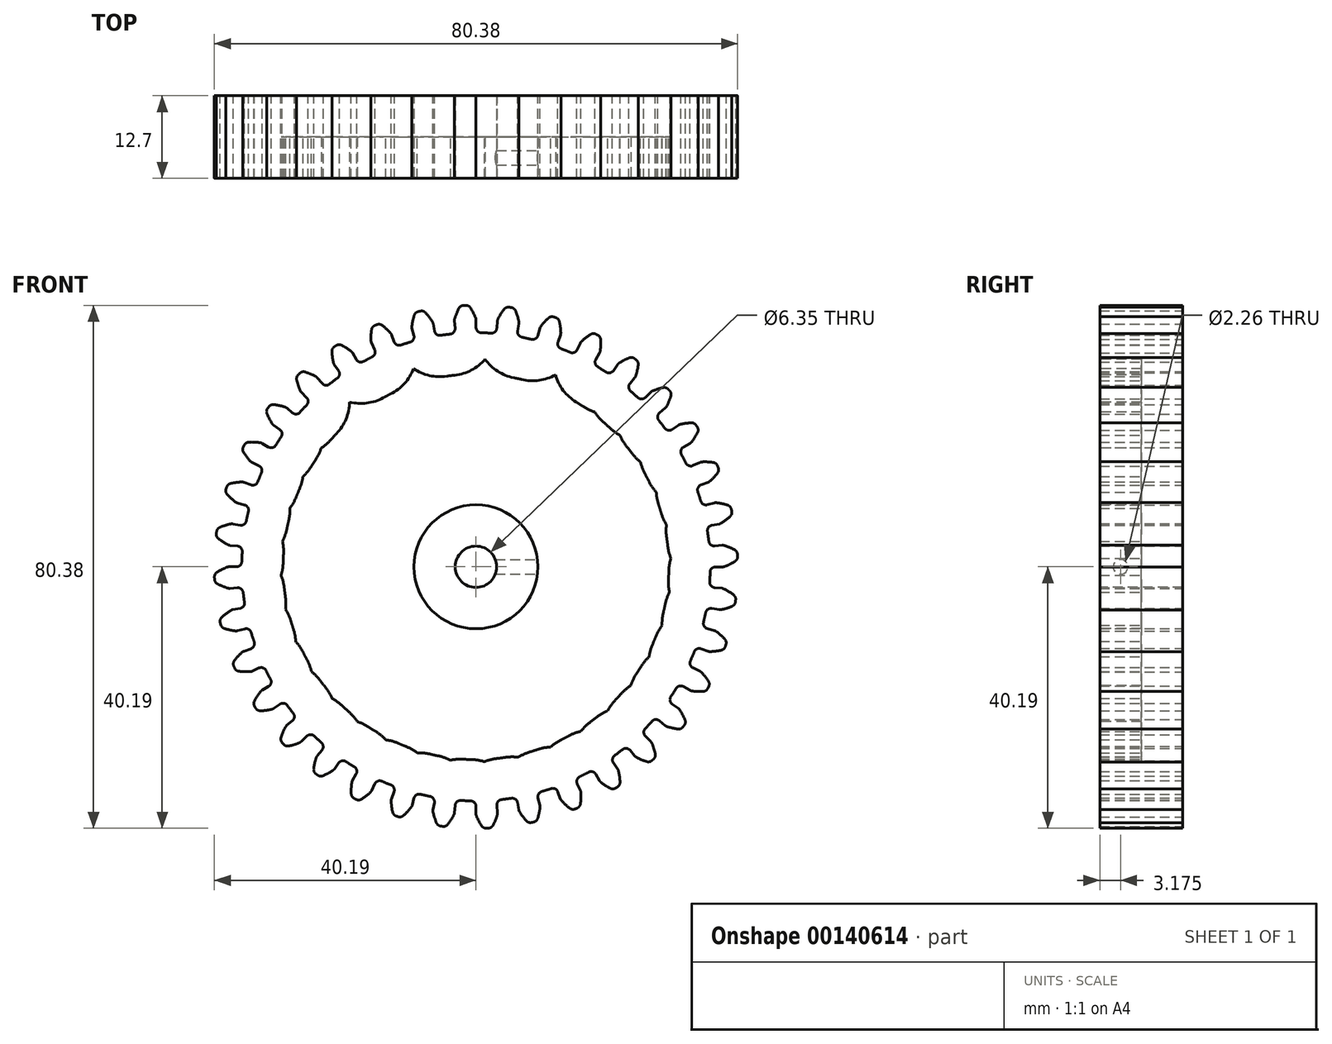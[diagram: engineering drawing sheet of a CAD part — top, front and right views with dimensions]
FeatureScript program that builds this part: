
annotation { "Feature Type Name" : "Feature", "Feature Type Description" : "" }
export const myFeature = defineFeature(function(context is Context, id is Id, definition is map)
    precondition{}
    {
        {
            var Q0;
            Q0=qCreatedBy(makeId("Front.planeOp"),FACE);
            var sketch = newSketch(context, id + "F0", { "sketchPlane" : qUnion([Q0])});
            skArc(sketch, "E0", {"start": v(-3.95, 35.77) * mm, "mid": v(-4.7, 35.68) * mm, "end": v(-5.45, 35.57) * mm});
            skArc(sketch, "E1", {"start": v(-0.05, 38.25) * mm, "mid": v(-0.42, 39.05) * mm, "end": v(-0.85, 39.8) * mm});
            skArc(sketch, "E2.trimOffspring", {"start": v(-1.58, 40.19) * mm, "mid": v(-1.67, 40.18) * mm, "end": v(-1.75, 40.18) * mm});
            skLineSegment(sketch, "E3", {"start": v(0, 37.94) * mm, "end": v(0, 36.8) * mm});
            skArc(sketch, "E4.MirrorCS", {"start": v(-1.93, 40.17) * mm, "mid": v(-1.84, 40.17) * mm, "end": v(-1.75, 40.18) * mm});
            skArc(sketch, "E5.MirrorCS", {"start": v(-3.28, 38.11) * mm, "mid": v(-2.99, 38.93) * mm, "end": v(-2.62, 39.73) * mm});
            skLineSegment(sketch, "E6.MirrorCS", {"start": v(-3.31, 37.8) * mm, "end": v(-3.21, 36.66) * mm});
            skPoint(sketch, "E7.visualSharp", {"position": v(-3.33, 37.95) * mm});
            skArc(sketch, "E7.filletArc", {"start": v(-3.28, 38.11) * mm, "mid": v(-3.31, 37.96) * mm, "end": v(-3.31, 37.8) * mm});
            skPoint(sketch, "E8.visualSharp", {"position": v(0, 38.1) * mm});
            skArc(sketch, "E8.filletArc", {"start": v(0, 37.94) * mm, "mid": v(0, 38.1) * mm, "end": v(-0.05, 38.25) * mm});
            skPoint(sketch, "E9.visualSharp", {"position": v(-2.39, 40.15) * mm});
            skArc(sketch, "E9.filletArc", {"start": v(-1.93, 40.17) * mm, "mid": v(-2.33, 40.04) * mm, "end": v(-2.62, 39.73) * mm});
            skPoint(sketch, "E10.visualSharp", {"position": v(-1.12, 40.2) * mm});
            skArc(sketch, "E10.filletArc", {"start": v(-0.85, 39.8) * mm, "mid": v(-1.17, 40.1) * mm, "end": v(-1.58, 40.19) * mm});
            skPoint(sketch, "E11.visualSharp", {"position": v(-3.14, 35.85) * mm});
            skArc(sketch, "E11.filletArc", {"start": v(-3.95, 35.77) * mm, "mid": v(-3.4, 36.06) * mm, "end": v(-3.21, 36.66) * mm});
            skPoint(sketch, "E12.visualSharp", {"position": v(0, 35.98) * mm});
            skArc(sketch, "E12.filletArc", {"start": v(0, 36.8) * mm, "mid": v(0.24, 36.22) * mm, "end": v(0.81, 35.97) * mm});
            skArc(sketch, "E13.1.0", {"start": v(-10.1, 34.54) * mm, "mid": v(-9.6, 34.93) * mm, "end": v(-9.53, 35.54) * mm});
            skLineSegment(sketch, "E13.1.1", {"start": v(-9.83, 36.65) * mm, "end": v(-9.53, 35.54) * mm});
            skArc(sketch, "E13.1.2", {"start": v(-9.85, 36.96) * mm, "mid": v(-9.85, 36.8) * mm, "end": v(-9.83, 36.65) * mm});
            skArc(sketch, "E13.1.3", {"start": v(-9.85, 36.96) * mm, "mid": v(-9.7, 37.82) * mm, "end": v(-9.48, 38.67) * mm});
            skArc(sketch, "E13.1.4", {"start": v(-8.87, 39.23) * mm, "mid": v(-9.25, 39.03) * mm, "end": v(-9.48, 38.67) * mm});
            skArc(sketch, "E13.1.5", {"start": v(-8.87, 39.23) * mm, "mid": v(-8.79, 39.24) * mm, "end": v(-8.7, 39.26) * mm});
            skArc(sketch, "E13.1.6", {"start": v(-8.54, 39.3) * mm, "mid": v(-8.62, 39.28) * mm, "end": v(-8.7, 39.26) * mm});
            skArc(sketch, "E13.1.7", {"start": v(-7.75, 39.05) * mm, "mid": v(-8.11, 39.28) * mm, "end": v(-8.54, 39.3) * mm});
            skArc(sketch, "E13.1.8", {"start": v(-6.7, 37.66) * mm, "mid": v(-7.2, 38.38) * mm, "end": v(-7.75, 39.05) * mm});
            skArc(sketch, "E13.1.9", {"start": v(-6.58, 37.37) * mm, "mid": v(-6.62, 37.52) * mm, "end": v(-6.7, 37.66) * mm});
            skLineSegment(sketch, "E13.1.10", {"start": v(-6.58, 37.37) * mm, "end": v(-6.38, 36.24) * mm});
            skArc(sketch, "E13.1.11", {"start": v(-6.38, 36.24) * mm, "mid": v(-6.05, 35.71) * mm, "end": v(-5.45, 35.57) * mm});
            skArc(sketch, "E13.2.0", {"start": v(-15.94, 32.26) * mm, "mid": v(-15.53, 32.73) * mm, "end": v(-15.56, 33.35) * mm});
            skLineSegment(sketch, "E13.2.1", {"start": v(-16.04, 34.39) * mm, "end": v(-15.56, 33.35) * mm});
            skArc(sketch, "E13.2.2", {"start": v(-16.12, 34.7) * mm, "mid": v(-16.1, 34.53) * mm, "end": v(-16.04, 34.39) * mm});
            skArc(sketch, "E13.2.3", {"start": v(-16.12, 34.7) * mm, "mid": v(-16.12, 35.56) * mm, "end": v(-16.05, 36.44) * mm});
            skArc(sketch, "E13.2.4", {"start": v(-15.55, 37.09) * mm, "mid": v(-15.89, 36.83) * mm, "end": v(-16.05, 36.44) * mm});
            skArc(sketch, "E13.2.5", {"start": v(-15.55, 37.09) * mm, "mid": v(-15.47, 37.12) * mm, "end": v(-15.4, 37.16) * mm});
            skArc(sketch, "E13.2.6", {"start": v(-15.23, 37.22) * mm, "mid": v(-15.31, 37.19) * mm, "end": v(-15.4, 37.16) * mm});
            skArc(sketch, "E13.2.7", {"start": v(-14.42, 37.11) * mm, "mid": v(-14.8, 37.28) * mm, "end": v(-15.23, 37.22) * mm});
            skArc(sketch, "E13.2.8", {"start": v(-13.13, 35.93) * mm, "mid": v(-13.75, 36.55) * mm, "end": v(-14.42, 37.11) * mm});
            skArc(sketch, "E13.2.9", {"start": v(-12.97, 35.66) * mm, "mid": v(-13.04, 35.8) * mm, "end": v(-13.13, 35.93) * mm});
            skLineSegment(sketch, "E13.2.10", {"start": v(-12.97, 35.66) * mm, "end": v(-12.58, 34.58) * mm});
            skArc(sketch, "E13.2.11", {"start": v(-12.58, 34.58) * mm, "mid": v(-12.16, 34.12) * mm, "end": v(-11.54, 34.08) * mm});
            skArc(sketch, "E13.3.0", {"start": v(-21.3, 29) * mm, "mid": v(-20.97, 29.53) * mm, "end": v(-21.11, 30.14) * mm});
            skLineSegment(sketch, "E13.3.1", {"start": v(-21.77, 31.08) * mm, "end": v(-21.11, 30.14) * mm});
            skArc(sketch, "E13.3.2", {"start": v(-21.9, 31.37) * mm, "mid": v(-21.85, 31.21) * mm, "end": v(-21.77, 31.08) * mm});
            skArc(sketch, "E13.3.3", {"start": v(-21.9, 31.37) * mm, "mid": v(-22.05, 32.22) * mm, "end": v(-22.13, 33.1) * mm});
            skArc(sketch, "E13.3.4", {"start": v(-21.75, 33.83) * mm, "mid": v(-22.04, 33.51) * mm, "end": v(-22.13, 33.1) * mm});
            skArc(sketch, "E13.3.5", {"start": v(-21.75, 33.83) * mm, "mid": v(-21.68, 33.87) * mm, "end": v(-21.6, 33.92) * mm});
            skArc(sketch, "E13.3.6", {"start": v(-21.46, 34.01) * mm, "mid": v(-21.54, 33.96) * mm, "end": v(-21.6, 33.92) * mm});
            skArc(sketch, "E13.3.7", {"start": v(-20.64, 34.05) * mm, "mid": v(-21.06, 34.14) * mm, "end": v(-21.46, 34.01) * mm});
            skArc(sketch, "E13.3.8", {"start": v(-19.17, 33.1) * mm, "mid": v(-19.88, 33.6) * mm, "end": v(-20.64, 34.05) * mm});
            skArc(sketch, "E13.3.9", {"start": v(-18.97, 32.86) * mm, "mid": v(-19.06, 33) * mm, "end": v(-19.17, 33.1) * mm});
            skLineSegment(sketch, "E13.3.10", {"start": v(-18.97, 32.86) * mm, "end": v(-18.4, 31.87) * mm});
            skArc(sketch, "E13.3.11", {"start": v(-18.4, 31.87) * mm, "mid": v(-17.9, 31.5) * mm, "end": v(-17.28, 31.56) * mm});
            skArc(sketch, "E13.4.0", {"start": v(-26.01, 24.86) * mm, "mid": v(-25.78, 25.44) * mm, "end": v(-26.03, 26.02) * mm});
            skLineSegment(sketch, "E13.4.1", {"start": v(-26.84, 26.82) * mm, "end": v(-26.03, 26.02) * mm});
            skArc(sketch, "E13.4.2", {"start": v(-27.01, 27.09) * mm, "mid": v(-26.94, 26.95) * mm, "end": v(-26.84, 26.82) * mm});
            skArc(sketch, "E13.4.3", {"start": v(-27.01, 27.09) * mm, "mid": v(-27.32, 27.9) * mm, "end": v(-27.54, 28.75) * mm});
            skArc(sketch, "E13.4.4", {"start": v(-27.3, 29.53) * mm, "mid": v(-27.52, 29.17) * mm, "end": v(-27.54, 28.75) * mm});
            skArc(sketch, "E13.4.5", {"start": v(-27.3, 29.53) * mm, "mid": v(-27.23, 29.6) * mm, "end": v(-27.17, 29.65) * mm});
            skArc(sketch, "E13.4.6", {"start": v(-27.04, 29.77) * mm, "mid": v(-27.1, 29.7) * mm, "end": v(-27.17, 29.65) * mm});
            skArc(sketch, "E13.4.7", {"start": v(-26.24, 29.94) * mm, "mid": v(-26.66, 29.96) * mm, "end": v(-27.04, 29.77) * mm});
            skArc(sketch, "E13.4.8", {"start": v(-24.63, 29.27) * mm, "mid": v(-25.42, 29.64) * mm, "end": v(-26.24, 29.94) * mm});
            skArc(sketch, "E13.4.9", {"start": v(-24.38, 29.07) * mm, "mid": v(-24.5, 29.18) * mm, "end": v(-24.63, 29.27) * mm});
            skLineSegment(sketch, "E13.4.10", {"start": v(-24.38, 29.07) * mm, "end": v(-23.65, 28.2) * mm});
            skArc(sketch, "E13.4.11", {"start": v(-23.65, 28.2) * mm, "mid": v(-23.1, 27.9) * mm, "end": v(-22.5, 28.08) * mm});
            skArc(sketch, "E13.5.0", {"start": v(-29.94, 19.97) * mm, "mid": v(-29.81, 20.58) * mm, "end": v(-30.15, 21.1) * mm});
            skLineSegment(sketch, "E13.5.1", {"start": v(-31.09, 21.76) * mm, "end": v(-30.15, 21.1) * mm});
            skArc(sketch, "E13.5.2", {"start": v(-31.3, 21.98) * mm, "mid": v(-31.2, 21.86) * mm, "end": v(-31.09, 21.76) * mm});
            skArc(sketch, "E13.5.3", {"start": v(-31.3, 21.98) * mm, "mid": v(-31.75, 22.74) * mm, "end": v(-32.12, 23.53) * mm});
            skArc(sketch, "E13.5.4", {"start": v(-32.01, 24.34) * mm, "mid": v(-32.17, 23.95) * mm, "end": v(-32.12, 23.53) * mm});
            skArc(sketch, "E13.5.5", {"start": v(-32.01, 24.34) * mm, "mid": v(-31.96, 24.41) * mm, "end": v(-31.9, 24.48) * mm});
            skArc(sketch, "E13.5.6", {"start": v(-31.8, 24.62) * mm, "mid": v(-31.85, 24.55) * mm, "end": v(-31.9, 24.48) * mm});
            skArc(sketch, "E13.5.7", {"start": v(-31.04, 24.93) * mm, "mid": v(-31.46, 24.88) * mm, "end": v(-31.8, 24.62) * mm});
            skArc(sketch, "E13.5.8", {"start": v(-29.34, 24.55) * mm, "mid": v(-30.18, 24.78) * mm, "end": v(-31.04, 24.93) * mm});
            skArc(sketch, "E13.5.9", {"start": v(-29.06, 24.4) * mm, "mid": v(-29.2, 24.48) * mm, "end": v(-29.34, 24.55) * mm});
            skLineSegment(sketch, "E13.5.10", {"start": v(-29.06, 24.4) * mm, "end": v(-28.19, 23.66) * mm});
            skArc(sketch, "E13.5.11", {"start": v(-28.19, 23.66) * mm, "mid": v(-27.6, 23.47) * mm, "end": v(-27.03, 23.75) * mm});
            skArc(sketch, "E13.6.0", {"start": v(-32.95, 14.47) * mm, "mid": v(-32.93, 15.09) * mm, "end": v(-33.35, 15.55) * mm});
            skLineSegment(sketch, "E13.6.1", {"start": v(-34.4, 16.03) * mm, "end": v(-33.35, 15.55) * mm});
            skArc(sketch, "E13.6.2", {"start": v(-34.65, 16.21) * mm, "mid": v(-34.53, 16.1) * mm, "end": v(-34.4, 16.03) * mm});
            skArc(sketch, "E13.6.3", {"start": v(-34.65, 16.21) * mm, "mid": v(-35.21, 16.88) * mm, "end": v(-35.71, 17.6) * mm});
            skArc(sketch, "E13.6.4", {"start": v(-35.75, 18.42) * mm, "mid": v(-35.84, 18) * mm, "end": v(-35.71, 17.6) * mm});
            skArc(sketch, "E13.6.5", {"start": v(-35.75, 18.42) * mm, "mid": v(-35.71, 18.5) * mm, "end": v(-35.67, 18.57) * mm});
            skArc(sketch, "E13.6.6", {"start": v(-35.6, 18.72) * mm, "mid": v(-35.63, 18.65) * mm, "end": v(-35.67, 18.57) * mm});
            skArc(sketch, "E13.6.7", {"start": v(-34.9, 19.16) * mm, "mid": v(-35.3, 19.04) * mm, "end": v(-35.6, 18.72) * mm});
            skArc(sketch, "E13.6.8", {"start": v(-33.15, 19.08) * mm, "mid": v(-34.02, 19.16) * mm, "end": v(-34.9, 19.16) * mm});
            skArc(sketch, "E13.6.9", {"start": v(-32.86, 18.98) * mm, "mid": v(-33, 19.04) * mm, "end": v(-33.15, 19.08) * mm});
            skLineSegment(sketch, "E13.6.10", {"start": v(-32.86, 18.98) * mm, "end": v(-31.87, 18.4) * mm});
            skArc(sketch, "E13.6.11", {"start": v(-31.87, 18.4) * mm, "mid": v(-31.25, 18.32) * mm, "end": v(-30.75, 18.7) * mm});
            skArc(sketch, "E13.7.0", {"start": v(-34.96, 8.52) * mm, "mid": v(-35.05, 9.14) * mm, "end": v(-35.55, 9.52) * mm});
            skLineSegment(sketch, "E13.7.1", {"start": v(-36.65, 9.81) * mm, "end": v(-35.55, 9.52) * mm});
            skArc(sketch, "E13.7.2", {"start": v(-36.94, 9.95) * mm, "mid": v(-36.8, 9.87) * mm, "end": v(-36.65, 9.81) * mm});
            skArc(sketch, "E13.7.3", {"start": v(-36.94, 9.95) * mm, "mid": v(-37.6, 10.5) * mm, "end": v(-38.23, 11.13) * mm});
            skArc(sketch, "E13.7.4", {"start": v(-38.4, 11.93) * mm, "mid": v(-38.42, 11.5) * mm, "end": v(-38.23, 11.13) * mm});
            skArc(sketch, "E13.7.5", {"start": v(-38.4, 11.93) * mm, "mid": v(-38.38, 12.01) * mm, "end": v(-38.36, 12.1) * mm});
            skArc(sketch, "E13.7.6", {"start": v(-38.3, 12.26) * mm, "mid": v(-38.33, 12.18) * mm, "end": v(-38.36, 12.1) * mm});
            skArc(sketch, "E13.7.7", {"start": v(-37.7, 12.81) * mm, "mid": v(-38.07, 12.62) * mm, "end": v(-38.3, 12.26) * mm});
            skArc(sketch, "E13.7.8", {"start": v(-35.96, 13.03) * mm, "mid": v(-36.83, 12.96) * mm, "end": v(-37.7, 12.81) * mm});
            skArc(sketch, "E13.7.9", {"start": v(-35.65, 12.98) * mm, "mid": v(-35.8, 13.02) * mm, "end": v(-35.96, 13.03) * mm});
            skLineSegment(sketch, "E13.7.10", {"start": v(-35.65, 12.98) * mm, "end": v(-34.58, 12.6) * mm});
            skArc(sketch, "E13.7.11", {"start": v(-34.58, 12.6) * mm, "mid": v(-33.95, 12.62) * mm, "end": v(-33.53, 13.07) * mm});
            skArc(sketch, "E13.8.0", {"start": v(-35.9, 2.32) * mm, "mid": v(-36.1, 2.92) * mm, "end": v(-36.66, 3.2) * mm});
            skLineSegment(sketch, "E13.8.1", {"start": v(-37.8, 3.3) * mm, "end": v(-36.66, 3.2) * mm});
            skArc(sketch, "E13.8.2", {"start": v(-38.1, 3.39) * mm, "mid": v(-37.96, 3.33) * mm, "end": v(-37.8, 3.3) * mm});
            skArc(sketch, "E13.8.3", {"start": v(-38.1, 3.39) * mm, "mid": v(-38.86, 3.82) * mm, "end": v(-39.58, 4.32) * mm});
            skArc(sketch, "E13.8.4", {"start": v(-39.9, 5.08) * mm, "mid": v(-39.84, 4.66) * mm, "end": v(-39.58, 4.32) * mm});
            skArc(sketch, "E13.8.5", {"start": v(-39.9, 5.08) * mm, "mid": v(-39.88, 5.16) * mm, "end": v(-39.87, 5.25) * mm});
            skArc(sketch, "E13.8.6", {"start": v(-39.85, 5.42) * mm, "mid": v(-39.86, 5.34) * mm, "end": v(-39.87, 5.25) * mm});
            skArc(sketch, "E13.8.7", {"start": v(-39.35, 6.07) * mm, "mid": v(-39.69, 5.81) * mm, "end": v(-39.85, 5.42) * mm});
            skArc(sketch, "E13.8.8", {"start": v(-37.68, 6.6) * mm, "mid": v(-38.53, 6.37) * mm, "end": v(-39.35, 6.07) * mm});
            skArc(sketch, "E13.8.9", {"start": v(-37.37, 6.6) * mm, "mid": v(-37.52, 6.6) * mm, "end": v(-37.68, 6.6) * mm});
            skLineSegment(sketch, "E13.8.10", {"start": v(-37.37, 6.6) * mm, "end": v(-36.24, 6.4) * mm});
            skArc(sketch, "E13.8.11", {"start": v(-36.24, 6.4) * mm, "mid": v(-35.63, 6.53) * mm, "end": v(-35.29, 7.05) * mm});
            skArc(sketch, "E13.9.0", {"start": v(-35.77, -3.95) * mm, "mid": v(-36.06, -3.4) * mm, "end": v(-36.66, -3.21) * mm});
            skLineSegment(sketch, "E13.9.1", {"start": v(-37.8, -3.31) * mm, "end": v(-36.66, -3.21) * mm});
            skArc(sketch, "E13.9.2", {"start": v(-38.11, -3.28) * mm, "mid": v(-37.96, -3.31) * mm, "end": v(-37.8, -3.31) * mm});
            skArc(sketch, "E13.9.3", {"start": v(-38.11, -3.28) * mm, "mid": v(-38.93, -2.99) * mm, "end": v(-39.73, -2.62) * mm});
            skArc(sketch, "E13.9.4", {"start": v(-40.17, -1.93) * mm, "mid": v(-40.04, -2.33) * mm, "end": v(-39.73, -2.62) * mm});
            skArc(sketch, "E13.9.5", {"start": v(-40.17, -1.93) * mm, "mid": v(-40.17, -1.84) * mm, "end": v(-40.18, -1.75) * mm});
            skArc(sketch, "E13.9.6", {"start": v(-40.19, -1.58) * mm, "mid": v(-40.18, -1.67) * mm, "end": v(-40.18, -1.75) * mm});
            skArc(sketch, "E13.9.7", {"start": v(-39.8, -0.85) * mm, "mid": v(-40.1, -1.17) * mm, "end": v(-40.19, -1.58) * mm});
            skArc(sketch, "E13.9.8", {"start": v(-38.25, -0.05) * mm, "mid": v(-39.05, -0.42) * mm, "end": v(-39.8, -0.85) * mm});
            skArc(sketch, "E13.9.9", {"start": v(-37.94, 0) * mm, "mid": v(-38.1, 0) * mm, "end": v(-38.25, -0.05) * mm});
            skLineSegment(sketch, "E13.9.10", {"start": v(-37.94, 0) * mm, "end": v(-36.8, 0) * mm});
            skArc(sketch, "E13.9.11", {"start": v(-36.8, 0) * mm, "mid": v(-36.22, 0.24) * mm, "end": v(-35.97, 0.81) * mm});
            skArc(sketch, "E13.10.0", {"start": v(-34.54, -10.1) * mm, "mid": v(-34.93, -9.6) * mm, "end": v(-35.54, -9.53) * mm});
            skLineSegment(sketch, "E13.10.1", {"start": v(-36.65, -9.83) * mm, "end": v(-35.54, -9.53) * mm});
            skArc(sketch, "E13.10.2", {"start": v(-36.96, -9.85) * mm, "mid": v(-36.8, -9.85) * mm, "end": v(-36.65, -9.83) * mm});
            skArc(sketch, "E13.10.3", {"start": v(-36.96, -9.85) * mm, "mid": v(-37.82, -9.7) * mm, "end": v(-38.67, -9.48) * mm});
            skArc(sketch, "E13.10.4", {"start": v(-39.23, -8.87) * mm, "mid": v(-39.03, -9.25) * mm, "end": v(-38.67, -9.48) * mm});
            skArc(sketch, "E13.10.5", {"start": v(-39.23, -8.87) * mm, "mid": v(-39.24, -8.79) * mm, "end": v(-39.26, -8.7) * mm});
            skArc(sketch, "E13.10.6", {"start": v(-39.3, -8.54) * mm, "mid": v(-39.28, -8.62) * mm, "end": v(-39.26, -8.7) * mm});
            skArc(sketch, "E13.10.7", {"start": v(-39.05, -7.75) * mm, "mid": v(-39.28, -8.11) * mm, "end": v(-39.3, -8.54) * mm});
            skArc(sketch, "E13.10.8", {"start": v(-37.66, -6.7) * mm, "mid": v(-38.38, -7.2) * mm, "end": v(-39.05, -7.75) * mm});
            skArc(sketch, "E13.10.9", {"start": v(-37.37, -6.58) * mm, "mid": v(-37.52, -6.62) * mm, "end": v(-37.66, -6.7) * mm});
            skLineSegment(sketch, "E13.10.10", {"start": v(-37.37, -6.58) * mm, "end": v(-36.24, -6.38) * mm});
            skArc(sketch, "E13.10.11", {"start": v(-36.24, -6.38) * mm, "mid": v(-35.71, -6.05) * mm, "end": v(-35.57, -5.45) * mm});
            skArc(sketch, "E13.11.0", {"start": v(-32.26, -15.94) * mm, "mid": v(-32.73, -15.53) * mm, "end": v(-33.35, -15.56) * mm});
            skLineSegment(sketch, "E13.11.1", {"start": v(-34.39, -16.04) * mm, "end": v(-33.35, -15.56) * mm});
            skArc(sketch, "E13.11.2", {"start": v(-34.7, -16.12) * mm, "mid": v(-34.53, -16.1) * mm, "end": v(-34.39, -16.04) * mm});
            skArc(sketch, "E13.11.3", {"start": v(-34.7, -16.12) * mm, "mid": v(-35.56, -16.12) * mm, "end": v(-36.44, -16.05) * mm});
            skArc(sketch, "E13.11.4", {"start": v(-37.09, -15.55) * mm, "mid": v(-36.83, -15.89) * mm, "end": v(-36.44, -16.05) * mm});
            skArc(sketch, "E13.11.5", {"start": v(-37.09, -15.55) * mm, "mid": v(-37.12, -15.47) * mm, "end": v(-37.16, -15.4) * mm});
            skArc(sketch, "E13.11.6", {"start": v(-37.22, -15.23) * mm, "mid": v(-37.19, -15.31) * mm, "end": v(-37.16, -15.4) * mm});
            skArc(sketch, "E13.11.7", {"start": v(-37.11, -14.42) * mm, "mid": v(-37.28, -14.8) * mm, "end": v(-37.22, -15.23) * mm});
            skArc(sketch, "E13.11.8", {"start": v(-35.93, -13.13) * mm, "mid": v(-36.55, -13.75) * mm, "end": v(-37.11, -14.42) * mm});
            skArc(sketch, "E13.11.9", {"start": v(-35.66, -12.97) * mm, "mid": v(-35.8, -13.04) * mm, "end": v(-35.93, -13.13) * mm});
            skLineSegment(sketch, "E13.11.10", {"start": v(-35.66, -12.97) * mm, "end": v(-34.58, -12.58) * mm});
            skArc(sketch, "E13.11.11", {"start": v(-34.58, -12.58) * mm, "mid": v(-34.12, -12.16) * mm, "end": v(-34.08, -11.54) * mm});
            skArc(sketch, "E13.12.0", {"start": v(-29, -21.3) * mm, "mid": v(-29.53, -20.97) * mm, "end": v(-30.14, -21.11) * mm});
            skLineSegment(sketch, "E13.12.1", {"start": v(-31.08, -21.77) * mm, "end": v(-30.14, -21.11) * mm});
            skArc(sketch, "E13.12.2", {"start": v(-31.37, -21.9) * mm, "mid": v(-31.21, -21.85) * mm, "end": v(-31.08, -21.77) * mm});
            skArc(sketch, "E13.12.3", {"start": v(-31.37, -21.9) * mm, "mid": v(-32.22, -22.05) * mm, "end": v(-33.1, -22.13) * mm});
            skArc(sketch, "E13.12.4", {"start": v(-33.83, -21.75) * mm, "mid": v(-33.51, -22.04) * mm, "end": v(-33.1, -22.13) * mm});
            skArc(sketch, "E13.12.5", {"start": v(-33.83, -21.75) * mm, "mid": v(-33.87, -21.68) * mm, "end": v(-33.92, -21.6) * mm});
            skArc(sketch, "E13.12.6", {"start": v(-34.01, -21.46) * mm, "mid": v(-33.96, -21.54) * mm, "end": v(-33.92, -21.6) * mm});
            skArc(sketch, "E13.12.7", {"start": v(-34.05, -20.64) * mm, "mid": v(-34.14, -21.06) * mm, "end": v(-34.01, -21.46) * mm});
            skArc(sketch, "E13.12.8", {"start": v(-33.1, -19.17) * mm, "mid": v(-33.6, -19.88) * mm, "end": v(-34.05, -20.64) * mm});
            skArc(sketch, "E13.12.9", {"start": v(-32.86, -18.97) * mm, "mid": v(-33, -19.06) * mm, "end": v(-33.1, -19.17) * mm});
            skLineSegment(sketch, "E13.12.10", {"start": v(-32.86, -18.97) * mm, "end": v(-31.87, -18.4) * mm});
            skArc(sketch, "E13.12.11", {"start": v(-31.87, -18.4) * mm, "mid": v(-31.5, -17.9) * mm, "end": v(-31.56, -17.28) * mm});
            skArc(sketch, "E13.13.0", {"start": v(-24.86, -26.01) * mm, "mid": v(-25.44, -25.78) * mm, "end": v(-26.02, -26.03) * mm});
            skLineSegment(sketch, "E13.13.1", {"start": v(-26.82, -26.84) * mm, "end": v(-26.02, -26.03) * mm});
            skArc(sketch, "E13.13.2", {"start": v(-27.09, -27.01) * mm, "mid": v(-26.95, -26.94) * mm, "end": v(-26.82, -26.84) * mm});
            skArc(sketch, "E13.13.3", {"start": v(-27.09, -27.01) * mm, "mid": v(-27.9, -27.32) * mm, "end": v(-28.75, -27.54) * mm});
            skArc(sketch, "E13.13.4", {"start": v(-29.53, -27.3) * mm, "mid": v(-29.17, -27.52) * mm, "end": v(-28.75, -27.54) * mm});
            skArc(sketch, "E13.13.5", {"start": v(-29.53, -27.3) * mm, "mid": v(-29.6, -27.23) * mm, "end": v(-29.65, -27.17) * mm});
            skArc(sketch, "E13.13.6", {"start": v(-29.77, -27.04) * mm, "mid": v(-29.7, -27.1) * mm, "end": v(-29.65, -27.17) * mm});
            skArc(sketch, "E13.13.7", {"start": v(-29.94, -26.24) * mm, "mid": v(-29.96, -26.66) * mm, "end": v(-29.77, -27.04) * mm});
            skArc(sketch, "E13.13.8", {"start": v(-29.27, -24.63) * mm, "mid": v(-29.64, -25.42) * mm, "end": v(-29.94, -26.24) * mm});
            skArc(sketch, "E13.13.9", {"start": v(-29.07, -24.38) * mm, "mid": v(-29.18, -24.5) * mm, "end": v(-29.27, -24.63) * mm});
            skLineSegment(sketch, "E13.13.10", {"start": v(-29.07, -24.38) * mm, "end": v(-28.2, -23.65) * mm});
            skArc(sketch, "E13.13.11", {"start": v(-28.2, -23.65) * mm, "mid": v(-27.9, -23.1) * mm, "end": v(-28.08, -22.5) * mm});
            skArc(sketch, "E13.14.0", {"start": v(-19.97, -29.94) * mm, "mid": v(-20.58, -29.81) * mm, "end": v(-21.1, -30.15) * mm});
            skLineSegment(sketch, "E13.14.1", {"start": v(-21.76, -31.09) * mm, "end": v(-21.1, -30.15) * mm});
            skArc(sketch, "E13.14.2", {"start": v(-21.98, -31.3) * mm, "mid": v(-21.86, -31.2) * mm, "end": v(-21.76, -31.09) * mm});
            skArc(sketch, "E13.14.3", {"start": v(-21.98, -31.3) * mm, "mid": v(-22.74, -31.75) * mm, "end": v(-23.53, -32.12) * mm});
            skArc(sketch, "E13.14.4", {"start": v(-24.34, -32.01) * mm, "mid": v(-23.95, -32.17) * mm, "end": v(-23.53, -32.12) * mm});
            skArc(sketch, "E13.14.5", {"start": v(-24.34, -32.01) * mm, "mid": v(-24.41, -31.96) * mm, "end": v(-24.48, -31.9) * mm});
            skArc(sketch, "E13.14.6", {"start": v(-24.62, -31.8) * mm, "mid": v(-24.55, -31.85) * mm, "end": v(-24.48, -31.9) * mm});
            skArc(sketch, "E13.14.7", {"start": v(-24.93, -31.04) * mm, "mid": v(-24.88, -31.46) * mm, "end": v(-24.62, -31.8) * mm});
            skArc(sketch, "E13.14.8", {"start": v(-24.55, -29.34) * mm, "mid": v(-24.78, -30.18) * mm, "end": v(-24.93, -31.04) * mm});
            skArc(sketch, "E13.14.9", {"start": v(-24.4, -29.06) * mm, "mid": v(-24.48, -29.2) * mm, "end": v(-24.55, -29.34) * mm});
            skLineSegment(sketch, "E13.14.10", {"start": v(-24.4, -29.06) * mm, "end": v(-23.66, -28.19) * mm});
            skArc(sketch, "E13.14.11", {"start": v(-23.66, -28.19) * mm, "mid": v(-23.47, -27.6) * mm, "end": v(-23.75, -27.03) * mm});
            skArc(sketch, "E13.15.0", {"start": v(-14.47, -32.95) * mm, "mid": v(-15.09, -32.93) * mm, "end": v(-15.55, -33.35) * mm});
            skLineSegment(sketch, "E13.15.1", {"start": v(-16.03, -34.4) * mm, "end": v(-15.55, -33.35) * mm});
            skArc(sketch, "E13.15.2", {"start": v(-16.21, -34.65) * mm, "mid": v(-16.1, -34.53) * mm, "end": v(-16.03, -34.4) * mm});
            skArc(sketch, "E13.15.3", {"start": v(-16.21, -34.65) * mm, "mid": v(-16.88, -35.21) * mm, "end": v(-17.6, -35.71) * mm});
            skArc(sketch, "E13.15.4", {"start": v(-18.42, -35.75) * mm, "mid": v(-18, -35.84) * mm, "end": v(-17.6, -35.71) * mm});
            skArc(sketch, "E13.15.5", {"start": v(-18.42, -35.75) * mm, "mid": v(-18.5, -35.71) * mm, "end": v(-18.57, -35.67) * mm});
            skArc(sketch, "E13.15.6", {"start": v(-18.72, -35.6) * mm, "mid": v(-18.65, -35.63) * mm, "end": v(-18.57, -35.67) * mm});
            skArc(sketch, "E13.15.7", {"start": v(-19.16, -34.9) * mm, "mid": v(-19.04, -35.3) * mm, "end": v(-18.72, -35.6) * mm});
            skArc(sketch, "E13.15.8", {"start": v(-19.08, -33.15) * mm, "mid": v(-19.16, -34.02) * mm, "end": v(-19.16, -34.9) * mm});
            skArc(sketch, "E13.15.9", {"start": v(-18.98, -32.86) * mm, "mid": v(-19.04, -33) * mm, "end": v(-19.08, -33.15) * mm});
            skLineSegment(sketch, "E13.15.10", {"start": v(-18.98, -32.86) * mm, "end": v(-18.4, -31.87) * mm});
            skArc(sketch, "E13.15.11", {"start": v(-18.4, -31.87) * mm, "mid": v(-18.32, -31.25) * mm, "end": v(-18.7, -30.75) * mm});
            skArc(sketch, "E13.16.0", {"start": v(-8.52, -34.96) * mm, "mid": v(-9.14, -35.05) * mm, "end": v(-9.52, -35.55) * mm});
            skLineSegment(sketch, "E13.16.1", {"start": v(-9.81, -36.65) * mm, "end": v(-9.52, -35.55) * mm});
            skArc(sketch, "E13.16.2", {"start": v(-9.95, -36.94) * mm, "mid": v(-9.87, -36.8) * mm, "end": v(-9.81, -36.65) * mm});
            skArc(sketch, "E13.16.3", {"start": v(-9.95, -36.94) * mm, "mid": v(-10.5, -37.6) * mm, "end": v(-11.13, -38.23) * mm});
            skArc(sketch, "E13.16.4", {"start": v(-11.93, -38.4) * mm, "mid": v(-11.5, -38.42) * mm, "end": v(-11.13, -38.23) * mm});
            skArc(sketch, "E13.16.5", {"start": v(-11.93, -38.4) * mm, "mid": v(-12.01, -38.38) * mm, "end": v(-12.1, -38.36) * mm});
            skArc(sketch, "E13.16.6", {"start": v(-12.26, -38.3) * mm, "mid": v(-12.18, -38.33) * mm, "end": v(-12.1, -38.36) * mm});
            skArc(sketch, "E13.16.7", {"start": v(-12.81, -37.7) * mm, "mid": v(-12.62, -38.07) * mm, "end": v(-12.26, -38.3) * mm});
            skArc(sketch, "E13.16.8", {"start": v(-13.03, -35.96) * mm, "mid": v(-12.96, -36.83) * mm, "end": v(-12.81, -37.7) * mm});
            skArc(sketch, "E13.16.9", {"start": v(-12.98, -35.65) * mm, "mid": v(-13.02, -35.8) * mm, "end": v(-13.03, -35.96) * mm});
            skLineSegment(sketch, "E13.16.10", {"start": v(-12.98, -35.65) * mm, "end": v(-12.6, -34.58) * mm});
            skArc(sketch, "E13.16.11", {"start": v(-12.6, -34.58) * mm, "mid": v(-12.62, -33.95) * mm, "end": v(-13.07, -33.53) * mm});
            skArc(sketch, "E13.17.0", {"start": v(-2.32, -35.9) * mm, "mid": v(-2.92, -36.1) * mm, "end": v(-3.2, -36.66) * mm});
            skLineSegment(sketch, "E13.17.1", {"start": v(-3.3, -37.8) * mm, "end": v(-3.2, -36.66) * mm});
            skArc(sketch, "E13.17.2", {"start": v(-3.39, -38.1) * mm, "mid": v(-3.33, -37.96) * mm, "end": v(-3.3, -37.8) * mm});
            skArc(sketch, "E13.17.3", {"start": v(-3.39, -38.1) * mm, "mid": v(-3.82, -38.86) * mm, "end": v(-4.32, -39.58) * mm});
            skArc(sketch, "E13.17.4", {"start": v(-5.08, -39.9) * mm, "mid": v(-4.66, -39.84) * mm, "end": v(-4.32, -39.58) * mm});
            skArc(sketch, "E13.17.5", {"start": v(-5.08, -39.9) * mm, "mid": v(-5.16, -39.88) * mm, "end": v(-5.25, -39.87) * mm});
            skArc(sketch, "E13.17.6", {"start": v(-5.42, -39.85) * mm, "mid": v(-5.34, -39.86) * mm, "end": v(-5.25, -39.87) * mm});
            skArc(sketch, "E13.17.7", {"start": v(-6.07, -39.35) * mm, "mid": v(-5.81, -39.69) * mm, "end": v(-5.42, -39.85) * mm});
            skArc(sketch, "E13.17.8", {"start": v(-6.6, -37.68) * mm, "mid": v(-6.37, -38.53) * mm, "end": v(-6.07, -39.35) * mm});
            skArc(sketch, "E13.17.9", {"start": v(-6.6, -37.37) * mm, "mid": v(-6.6, -37.52) * mm, "end": v(-6.6, -37.68) * mm});
            skLineSegment(sketch, "E13.17.10", {"start": v(-6.6, -37.37) * mm, "end": v(-6.4, -36.24) * mm});
            skArc(sketch, "E13.17.11", {"start": v(-6.4, -36.24) * mm, "mid": v(-6.53, -35.63) * mm, "end": v(-7.05, -35.29) * mm});
            skArc(sketch, "E13.18.0", {"start": v(3.95, -35.77) * mm, "mid": v(3.4, -36.06) * mm, "end": v(3.21, -36.66) * mm});
            skLineSegment(sketch, "E13.18.1", {"start": v(3.31, -37.8) * mm, "end": v(3.21, -36.66) * mm});
            skArc(sketch, "E13.18.2", {"start": v(3.28, -38.11) * mm, "mid": v(3.31, -37.96) * mm, "end": v(3.31, -37.8) * mm});
            skArc(sketch, "E13.18.3", {"start": v(3.28, -38.11) * mm, "mid": v(2.99, -38.93) * mm, "end": v(2.62, -39.73) * mm});
            skArc(sketch, "E13.18.4", {"start": v(1.93, -40.17) * mm, "mid": v(2.33, -40.04) * mm, "end": v(2.62, -39.73) * mm});
            skArc(sketch, "E13.18.5", {"start": v(1.93, -40.17) * mm, "mid": v(1.84, -40.17) * mm, "end": v(1.75, -40.18) * mm});
            skArc(sketch, "E13.18.6", {"start": v(1.58, -40.19) * mm, "mid": v(1.67, -40.18) * mm, "end": v(1.75, -40.18) * mm});
            skArc(sketch, "E13.18.7", {"start": v(0.85, -39.8) * mm, "mid": v(1.17, -40.1) * mm, "end": v(1.58, -40.19) * mm});
            skArc(sketch, "E13.18.8", {"start": v(0.05, -38.25) * mm, "mid": v(0.42, -39.05) * mm, "end": v(0.85, -39.8) * mm});
            skArc(sketch, "E13.18.9", {"start": v(0, -37.94) * mm, "mid": v(0, -38.1) * mm, "end": v(0.05, -38.25) * mm});
            skLineSegment(sketch, "E13.18.10", {"start": v(0, -37.94) * mm, "end": v(0, -36.8) * mm});
            skArc(sketch, "E13.18.11", {"start": v(0, -36.8) * mm, "mid": v(-0.24, -36.22) * mm, "end": v(-0.81, -35.97) * mm});
            skArc(sketch, "E13.19.0", {"start": v(10.1, -34.54) * mm, "mid": v(9.6, -34.93) * mm, "end": v(9.53, -35.54) * mm});
            skLineSegment(sketch, "E13.19.1", {"start": v(9.83, -36.65) * mm, "end": v(9.53, -35.54) * mm});
            skArc(sketch, "E13.19.2", {"start": v(9.85, -36.96) * mm, "mid": v(9.85, -36.8) * mm, "end": v(9.83, -36.65) * mm});
            skArc(sketch, "E13.19.3", {"start": v(9.85, -36.96) * mm, "mid": v(9.7, -37.82) * mm, "end": v(9.48, -38.67) * mm});
            skArc(sketch, "E13.19.4", {"start": v(8.87, -39.23) * mm, "mid": v(9.25, -39.03) * mm, "end": v(9.48, -38.67) * mm});
            skArc(sketch, "E13.19.5", {"start": v(8.87, -39.23) * mm, "mid": v(8.79, -39.24) * mm, "end": v(8.7, -39.26) * mm});
            skArc(sketch, "E13.19.6", {"start": v(8.54, -39.3) * mm, "mid": v(8.62, -39.28) * mm, "end": v(8.7, -39.26) * mm});
            skArc(sketch, "E13.19.7", {"start": v(7.75, -39.05) * mm, "mid": v(8.11, -39.28) * mm, "end": v(8.54, -39.3) * mm});
            skArc(sketch, "E13.19.8", {"start": v(6.7, -37.66) * mm, "mid": v(7.2, -38.38) * mm, "end": v(7.75, -39.05) * mm});
            skArc(sketch, "E13.19.9", {"start": v(6.58, -37.37) * mm, "mid": v(6.62, -37.52) * mm, "end": v(6.7, -37.66) * mm});
            skLineSegment(sketch, "E13.19.10", {"start": v(6.58, -37.37) * mm, "end": v(6.38, -36.24) * mm});
            skArc(sketch, "E13.19.11", {"start": v(6.38, -36.24) * mm, "mid": v(6.05, -35.71) * mm, "end": v(5.45, -35.57) * mm});
            skArc(sketch, "E13.20.0", {"start": v(15.94, -32.26) * mm, "mid": v(15.53, -32.73) * mm, "end": v(15.56, -33.35) * mm});
            skLineSegment(sketch, "E13.20.1", {"start": v(16.04, -34.39) * mm, "end": v(15.56, -33.35) * mm});
            skArc(sketch, "E13.20.2", {"start": v(16.12, -34.7) * mm, "mid": v(16.1, -34.53) * mm, "end": v(16.04, -34.39) * mm});
            skArc(sketch, "E13.20.3", {"start": v(16.12, -34.7) * mm, "mid": v(16.12, -35.56) * mm, "end": v(16.05, -36.44) * mm});
            skArc(sketch, "E13.20.4", {"start": v(15.55, -37.09) * mm, "mid": v(15.89, -36.83) * mm, "end": v(16.05, -36.44) * mm});
            skArc(sketch, "E13.20.5", {"start": v(15.55, -37.09) * mm, "mid": v(15.47, -37.12) * mm, "end": v(15.4, -37.16) * mm});
            skArc(sketch, "E13.20.6", {"start": v(15.23, -37.22) * mm, "mid": v(15.31, -37.19) * mm, "end": v(15.4, -37.16) * mm});
            skArc(sketch, "E13.20.7", {"start": v(14.42, -37.11) * mm, "mid": v(14.8, -37.28) * mm, "end": v(15.23, -37.22) * mm});
            skArc(sketch, "E13.20.8", {"start": v(13.13, -35.93) * mm, "mid": v(13.75, -36.55) * mm, "end": v(14.42, -37.11) * mm});
            skArc(sketch, "E13.20.9", {"start": v(12.97, -35.66) * mm, "mid": v(13.04, -35.8) * mm, "end": v(13.13, -35.93) * mm});
            skLineSegment(sketch, "E13.20.10", {"start": v(12.97, -35.66) * mm, "end": v(12.58, -34.58) * mm});
            skArc(sketch, "E13.20.11", {"start": v(12.58, -34.58) * mm, "mid": v(12.16, -34.12) * mm, "end": v(11.54, -34.08) * mm});
            skArc(sketch, "E13.21.0", {"start": v(21.3, -29) * mm, "mid": v(20.97, -29.53) * mm, "end": v(21.11, -30.14) * mm});
            skLineSegment(sketch, "E13.21.1", {"start": v(21.77, -31.08) * mm, "end": v(21.11, -30.14) * mm});
            skArc(sketch, "E13.21.2", {"start": v(21.9, -31.37) * mm, "mid": v(21.85, -31.21) * mm, "end": v(21.77, -31.08) * mm});
            skArc(sketch, "E13.21.3", {"start": v(21.9, -31.37) * mm, "mid": v(22.05, -32.22) * mm, "end": v(22.13, -33.1) * mm});
            skArc(sketch, "E13.21.4", {"start": v(21.75, -33.83) * mm, "mid": v(22.04, -33.51) * mm, "end": v(22.13, -33.1) * mm});
            skArc(sketch, "E13.21.5", {"start": v(21.75, -33.83) * mm, "mid": v(21.68, -33.87) * mm, "end": v(21.6, -33.92) * mm});
            skArc(sketch, "E13.21.6", {"start": v(21.46, -34.01) * mm, "mid": v(21.54, -33.96) * mm, "end": v(21.6, -33.92) * mm});
            skArc(sketch, "E13.21.7", {"start": v(20.64, -34.05) * mm, "mid": v(21.06, -34.14) * mm, "end": v(21.46, -34.01) * mm});
            skArc(sketch, "E13.21.8", {"start": v(19.17, -33.1) * mm, "mid": v(19.88, -33.6) * mm, "end": v(20.64, -34.05) * mm});
            skArc(sketch, "E13.21.9", {"start": v(18.97, -32.86) * mm, "mid": v(19.06, -33) * mm, "end": v(19.17, -33.1) * mm});
            skLineSegment(sketch, "E13.21.10", {"start": v(18.97, -32.86) * mm, "end": v(18.4, -31.87) * mm});
            skArc(sketch, "E13.21.11", {"start": v(18.4, -31.87) * mm, "mid": v(17.9, -31.5) * mm, "end": v(17.28, -31.56) * mm});
            skArc(sketch, "E13.22.0", {"start": v(26.01, -24.86) * mm, "mid": v(25.78, -25.44) * mm, "end": v(26.03, -26.02) * mm});
            skLineSegment(sketch, "E13.22.1", {"start": v(26.84, -26.82) * mm, "end": v(26.03, -26.02) * mm});
            skArc(sketch, "E13.22.2", {"start": v(27.01, -27.09) * mm, "mid": v(26.94, -26.95) * mm, "end": v(26.84, -26.82) * mm});
            skArc(sketch, "E13.22.3", {"start": v(27.01, -27.09) * mm, "mid": v(27.32, -27.9) * mm, "end": v(27.54, -28.75) * mm});
            skArc(sketch, "E13.22.4", {"start": v(27.3, -29.53) * mm, "mid": v(27.52, -29.17) * mm, "end": v(27.54, -28.75) * mm});
            skArc(sketch, "E13.22.5", {"start": v(27.3, -29.53) * mm, "mid": v(27.23, -29.6) * mm, "end": v(27.17, -29.65) * mm});
            skArc(sketch, "E13.22.6", {"start": v(27.04, -29.77) * mm, "mid": v(27.1, -29.7) * mm, "end": v(27.17, -29.65) * mm});
            skArc(sketch, "E13.22.7", {"start": v(26.24, -29.94) * mm, "mid": v(26.66, -29.96) * mm, "end": v(27.04, -29.77) * mm});
            skArc(sketch, "E13.22.8", {"start": v(24.63, -29.27) * mm, "mid": v(25.42, -29.64) * mm, "end": v(26.24, -29.94) * mm});
            skArc(sketch, "E13.22.9", {"start": v(24.38, -29.07) * mm, "mid": v(24.5, -29.18) * mm, "end": v(24.63, -29.27) * mm});
            skLineSegment(sketch, "E13.22.10", {"start": v(24.38, -29.07) * mm, "end": v(23.65, -28.2) * mm});
            skArc(sketch, "E13.22.11", {"start": v(23.65, -28.2) * mm, "mid": v(23.1, -27.9) * mm, "end": v(22.5, -28.08) * mm});
            skArc(sketch, "E13.23.0", {"start": v(29.94, -19.97) * mm, "mid": v(29.81, -20.58) * mm, "end": v(30.15, -21.1) * mm});
            skLineSegment(sketch, "E13.23.1", {"start": v(31.09, -21.76) * mm, "end": v(30.15, -21.1) * mm});
            skArc(sketch, "E13.23.2", {"start": v(31.3, -21.98) * mm, "mid": v(31.2, -21.86) * mm, "end": v(31.09, -21.76) * mm});
            skArc(sketch, "E13.23.3", {"start": v(31.3, -21.98) * mm, "mid": v(31.75, -22.74) * mm, "end": v(32.12, -23.53) * mm});
            skArc(sketch, "E13.23.4", {"start": v(32.01, -24.34) * mm, "mid": v(32.17, -23.95) * mm, "end": v(32.12, -23.53) * mm});
            skArc(sketch, "E13.23.5", {"start": v(32.01, -24.34) * mm, "mid": v(31.96, -24.41) * mm, "end": v(31.9, -24.48) * mm});
            skArc(sketch, "E13.23.6", {"start": v(31.8, -24.62) * mm, "mid": v(31.85, -24.55) * mm, "end": v(31.9, -24.48) * mm});
            skArc(sketch, "E13.23.7", {"start": v(31.04, -24.93) * mm, "mid": v(31.46, -24.88) * mm, "end": v(31.8, -24.62) * mm});
            skArc(sketch, "E13.23.8", {"start": v(29.34, -24.55) * mm, "mid": v(30.18, -24.78) * mm, "end": v(31.04, -24.93) * mm});
            skArc(sketch, "E13.23.9", {"start": v(29.06, -24.4) * mm, "mid": v(29.2, -24.48) * mm, "end": v(29.34, -24.55) * mm});
            skLineSegment(sketch, "E13.23.10", {"start": v(29.06, -24.4) * mm, "end": v(28.19, -23.66) * mm});
            skArc(sketch, "E13.23.11", {"start": v(28.19, -23.66) * mm, "mid": v(27.6, -23.47) * mm, "end": v(27.03, -23.75) * mm});
            skArc(sketch, "E13.24.0", {"start": v(32.95, -14.47) * mm, "mid": v(32.93, -15.09) * mm, "end": v(33.35, -15.55) * mm});
            skLineSegment(sketch, "E13.24.1", {"start": v(34.4, -16.03) * mm, "end": v(33.35, -15.55) * mm});
            skArc(sketch, "E13.24.2", {"start": v(34.65, -16.21) * mm, "mid": v(34.53, -16.1) * mm, "end": v(34.4, -16.03) * mm});
            skArc(sketch, "E13.24.3", {"start": v(34.65, -16.21) * mm, "mid": v(35.21, -16.88) * mm, "end": v(35.71, -17.6) * mm});
            skArc(sketch, "E13.24.4", {"start": v(35.75, -18.42) * mm, "mid": v(35.84, -18) * mm, "end": v(35.71, -17.6) * mm});
            skArc(sketch, "E13.24.5", {"start": v(35.75, -18.42) * mm, "mid": v(35.71, -18.5) * mm, "end": v(35.67, -18.57) * mm});
            skArc(sketch, "E13.24.6", {"start": v(35.6, -18.72) * mm, "mid": v(35.63, -18.65) * mm, "end": v(35.67, -18.57) * mm});
            skArc(sketch, "E13.24.7", {"start": v(34.9, -19.16) * mm, "mid": v(35.3, -19.04) * mm, "end": v(35.6, -18.72) * mm});
            skArc(sketch, "E13.24.8", {"start": v(33.15, -19.08) * mm, "mid": v(34.02, -19.16) * mm, "end": v(34.9, -19.16) * mm});
            skArc(sketch, "E13.24.9", {"start": v(32.86, -18.98) * mm, "mid": v(33, -19.04) * mm, "end": v(33.15, -19.08) * mm});
            skLineSegment(sketch, "E13.24.10", {"start": v(32.86, -18.98) * mm, "end": v(31.87, -18.4) * mm});
            skArc(sketch, "E13.24.11", {"start": v(31.87, -18.4) * mm, "mid": v(31.25, -18.32) * mm, "end": v(30.75, -18.7) * mm});
            skArc(sketch, "E13.25.0", {"start": v(34.96, -8.52) * mm, "mid": v(35.05, -9.14) * mm, "end": v(35.55, -9.52) * mm});
            skLineSegment(sketch, "E13.25.1", {"start": v(36.65, -9.81) * mm, "end": v(35.55, -9.52) * mm});
            skArc(sketch, "E13.25.2", {"start": v(36.94, -9.95) * mm, "mid": v(36.8, -9.87) * mm, "end": v(36.65, -9.81) * mm});
            skArc(sketch, "E13.25.3", {"start": v(36.94, -9.95) * mm, "mid": v(37.6, -10.5) * mm, "end": v(38.23, -11.13) * mm});
            skArc(sketch, "E13.25.4", {"start": v(38.4, -11.93) * mm, "mid": v(38.42, -11.5) * mm, "end": v(38.23, -11.13) * mm});
            skArc(sketch, "E13.25.5", {"start": v(38.4, -11.93) * mm, "mid": v(38.38, -12.01) * mm, "end": v(38.36, -12.1) * mm});
            skArc(sketch, "E13.25.6", {"start": v(38.3, -12.26) * mm, "mid": v(38.33, -12.18) * mm, "end": v(38.36, -12.1) * mm});
            skArc(sketch, "E13.25.7", {"start": v(37.7, -12.81) * mm, "mid": v(38.07, -12.62) * mm, "end": v(38.3, -12.26) * mm});
            skArc(sketch, "E13.25.8", {"start": v(35.96, -13.03) * mm, "mid": v(36.83, -12.96) * mm, "end": v(37.7, -12.81) * mm});
            skArc(sketch, "E13.25.9", {"start": v(35.65, -12.98) * mm, "mid": v(35.8, -13.02) * mm, "end": v(35.96, -13.03) * mm});
            skLineSegment(sketch, "E13.25.10", {"start": v(35.65, -12.98) * mm, "end": v(34.58, -12.6) * mm});
            skArc(sketch, "E13.25.11", {"start": v(34.58, -12.6) * mm, "mid": v(33.95, -12.62) * mm, "end": v(33.53, -13.07) * mm});
            skArc(sketch, "E13.26.0", {"start": v(35.9, -2.32) * mm, "mid": v(36.1, -2.92) * mm, "end": v(36.66, -3.2) * mm});
            skLineSegment(sketch, "E13.26.1", {"start": v(37.8, -3.3) * mm, "end": v(36.66, -3.2) * mm});
            skArc(sketch, "E13.26.2", {"start": v(38.1, -3.39) * mm, "mid": v(37.96, -3.33) * mm, "end": v(37.8, -3.3) * mm});
            skArc(sketch, "E13.26.3", {"start": v(38.1, -3.39) * mm, "mid": v(38.86, -3.82) * mm, "end": v(39.58, -4.32) * mm});
            skArc(sketch, "E13.26.4", {"start": v(39.9, -5.08) * mm, "mid": v(39.84, -4.66) * mm, "end": v(39.58, -4.32) * mm});
            skArc(sketch, "E13.26.5", {"start": v(39.9, -5.08) * mm, "mid": v(39.88, -5.16) * mm, "end": v(39.87, -5.25) * mm});
            skArc(sketch, "E13.26.6", {"start": v(39.85, -5.42) * mm, "mid": v(39.86, -5.34) * mm, "end": v(39.87, -5.25) * mm});
            skArc(sketch, "E13.26.7", {"start": v(39.35, -6.07) * mm, "mid": v(39.69, -5.81) * mm, "end": v(39.85, -5.42) * mm});
            skArc(sketch, "E13.26.8", {"start": v(37.68, -6.6) * mm, "mid": v(38.53, -6.37) * mm, "end": v(39.35, -6.07) * mm});
            skArc(sketch, "E13.26.9", {"start": v(37.37, -6.6) * mm, "mid": v(37.52, -6.6) * mm, "end": v(37.68, -6.6) * mm});
            skLineSegment(sketch, "E13.26.10", {"start": v(37.37, -6.6) * mm, "end": v(36.24, -6.4) * mm});
            skArc(sketch, "E13.26.11", {"start": v(36.24, -6.4) * mm, "mid": v(35.63, -6.53) * mm, "end": v(35.29, -7.05) * mm});
            skArc(sketch, "E13.27.0", {"start": v(35.77, 3.95) * mm, "mid": v(36.06, 3.4) * mm, "end": v(36.66, 3.21) * mm});
            skLineSegment(sketch, "E13.27.1", {"start": v(37.8, 3.31) * mm, "end": v(36.66, 3.21) * mm});
            skArc(sketch, "E13.27.2", {"start": v(38.11, 3.28) * mm, "mid": v(37.96, 3.31) * mm, "end": v(37.8, 3.31) * mm});
            skArc(sketch, "E13.27.3", {"start": v(38.11, 3.28) * mm, "mid": v(38.93, 2.99) * mm, "end": v(39.73, 2.62) * mm});
            skArc(sketch, "E13.27.4", {"start": v(40.17, 1.93) * mm, "mid": v(40.04, 2.33) * mm, "end": v(39.73, 2.62) * mm});
            skArc(sketch, "E13.27.5", {"start": v(40.17, 1.93) * mm, "mid": v(40.17, 1.84) * mm, "end": v(40.18, 1.75) * mm});
            skArc(sketch, "E13.27.6", {"start": v(40.19, 1.58) * mm, "mid": v(40.18, 1.67) * mm, "end": v(40.18, 1.75) * mm});
            skArc(sketch, "E13.27.7", {"start": v(39.8, 0.85) * mm, "mid": v(40.1, 1.17) * mm, "end": v(40.19, 1.58) * mm});
            skArc(sketch, "E13.27.8", {"start": v(38.25, 0.05) * mm, "mid": v(39.05, 0.42) * mm, "end": v(39.8, 0.85) * mm});
            skArc(sketch, "E13.27.9", {"start": v(37.94, 0) * mm, "mid": v(38.1, 0) * mm, "end": v(38.25, 0.05) * mm});
            skLineSegment(sketch, "E13.27.10", {"start": v(37.94, 0) * mm, "end": v(36.8, 0) * mm});
            skArc(sketch, "E13.27.11", {"start": v(36.8, 0) * mm, "mid": v(36.22, -0.24) * mm, "end": v(35.97, -0.81) * mm});
            skArc(sketch, "E13.28.0", {"start": v(34.54, 10.1) * mm, "mid": v(34.93, 9.6) * mm, "end": v(35.54, 9.53) * mm});
            skLineSegment(sketch, "E13.28.1", {"start": v(36.65, 9.83) * mm, "end": v(35.54, 9.53) * mm});
            skArc(sketch, "E13.28.2", {"start": v(36.96, 9.85) * mm, "mid": v(36.8, 9.85) * mm, "end": v(36.65, 9.83) * mm});
            skArc(sketch, "E13.28.3", {"start": v(36.96, 9.85) * mm, "mid": v(37.82, 9.7) * mm, "end": v(38.67, 9.48) * mm});
            skArc(sketch, "E13.28.4", {"start": v(39.23, 8.87) * mm, "mid": v(39.03, 9.25) * mm, "end": v(38.67, 9.48) * mm});
            skArc(sketch, "E13.28.5", {"start": v(39.23, 8.87) * mm, "mid": v(39.24, 8.79) * mm, "end": v(39.26, 8.7) * mm});
            skArc(sketch, "E13.28.6", {"start": v(39.3, 8.54) * mm, "mid": v(39.28, 8.62) * mm, "end": v(39.26, 8.7) * mm});
            skArc(sketch, "E13.28.7", {"start": v(39.05, 7.75) * mm, "mid": v(39.28, 8.11) * mm, "end": v(39.3, 8.54) * mm});
            skArc(sketch, "E13.28.8", {"start": v(37.66, 6.7) * mm, "mid": v(38.38, 7.2) * mm, "end": v(39.05, 7.75) * mm});
            skArc(sketch, "E13.28.9", {"start": v(37.37, 6.58) * mm, "mid": v(37.52, 6.62) * mm, "end": v(37.66, 6.7) * mm});
            skLineSegment(sketch, "E13.28.10", {"start": v(37.37, 6.58) * mm, "end": v(36.24, 6.38) * mm});
            skArc(sketch, "E13.28.11", {"start": v(36.24, 6.38) * mm, "mid": v(35.71, 6.05) * mm, "end": v(35.57, 5.45) * mm});
            skArc(sketch, "E13.29.0", {"start": v(32.26, 15.94) * mm, "mid": v(32.73, 15.53) * mm, "end": v(33.35, 15.56) * mm});
            skLineSegment(sketch, "E13.29.1", {"start": v(34.39, 16.04) * mm, "end": v(33.35, 15.56) * mm});
            skArc(sketch, "E13.29.2", {"start": v(34.7, 16.12) * mm, "mid": v(34.53, 16.1) * mm, "end": v(34.39, 16.04) * mm});
            skArc(sketch, "E13.29.3", {"start": v(34.7, 16.12) * mm, "mid": v(35.56, 16.12) * mm, "end": v(36.44, 16.05) * mm});
            skArc(sketch, "E13.29.4", {"start": v(37.09, 15.55) * mm, "mid": v(36.83, 15.89) * mm, "end": v(36.44, 16.05) * mm});
            skArc(sketch, "E13.29.5", {"start": v(37.09, 15.55) * mm, "mid": v(37.12, 15.47) * mm, "end": v(37.16, 15.4) * mm});
            skArc(sketch, "E13.29.6", {"start": v(37.22, 15.23) * mm, "mid": v(37.19, 15.31) * mm, "end": v(37.16, 15.4) * mm});
            skArc(sketch, "E13.29.7", {"start": v(37.11, 14.42) * mm, "mid": v(37.28, 14.8) * mm, "end": v(37.22, 15.23) * mm});
            skArc(sketch, "E13.29.8", {"start": v(35.93, 13.13) * mm, "mid": v(36.55, 13.75) * mm, "end": v(37.11, 14.42) * mm});
            skArc(sketch, "E13.29.9", {"start": v(35.66, 12.97) * mm, "mid": v(35.8, 13.04) * mm, "end": v(35.93, 13.13) * mm});
            skLineSegment(sketch, "E13.29.10", {"start": v(35.66, 12.97) * mm, "end": v(34.58, 12.58) * mm});
            skArc(sketch, "E13.29.11", {"start": v(34.58, 12.58) * mm, "mid": v(34.12, 12.16) * mm, "end": v(34.08, 11.54) * mm});
            skArc(sketch, "E13.30.0", {"start": v(29, 21.3) * mm, "mid": v(29.53, 20.97) * mm, "end": v(30.14, 21.11) * mm});
            skLineSegment(sketch, "E13.30.1", {"start": v(31.08, 21.77) * mm, "end": v(30.14, 21.11) * mm});
            skArc(sketch, "E13.30.2", {"start": v(31.37, 21.9) * mm, "mid": v(31.21, 21.85) * mm, "end": v(31.08, 21.77) * mm});
            skArc(sketch, "E13.30.3", {"start": v(31.37, 21.9) * mm, "mid": v(32.22, 22.05) * mm, "end": v(33.1, 22.13) * mm});
            skArc(sketch, "E13.30.4", {"start": v(33.83, 21.75) * mm, "mid": v(33.51, 22.04) * mm, "end": v(33.1, 22.13) * mm});
            skArc(sketch, "E13.30.5", {"start": v(33.83, 21.75) * mm, "mid": v(33.87, 21.68) * mm, "end": v(33.92, 21.6) * mm});
            skArc(sketch, "E13.30.6", {"start": v(34.01, 21.46) * mm, "mid": v(33.96, 21.54) * mm, "end": v(33.92, 21.6) * mm});
            skArc(sketch, "E13.30.7", {"start": v(34.05, 20.64) * mm, "mid": v(34.14, 21.06) * mm, "end": v(34.01, 21.46) * mm});
            skArc(sketch, "E13.30.8", {"start": v(33.1, 19.17) * mm, "mid": v(33.6, 19.88) * mm, "end": v(34.05, 20.64) * mm});
            skArc(sketch, "E13.30.9", {"start": v(32.86, 18.97) * mm, "mid": v(33, 19.06) * mm, "end": v(33.1, 19.17) * mm});
            skLineSegment(sketch, "E13.30.10", {"start": v(32.86, 18.97) * mm, "end": v(31.87, 18.4) * mm});
            skArc(sketch, "E13.30.11", {"start": v(31.87, 18.4) * mm, "mid": v(31.5, 17.9) * mm, "end": v(31.56, 17.28) * mm});
            skArc(sketch, "E13.31.0", {"start": v(24.86, 26.01) * mm, "mid": v(25.44, 25.78) * mm, "end": v(26.02, 26.03) * mm});
            skLineSegment(sketch, "E13.31.1", {"start": v(26.82, 26.84) * mm, "end": v(26.02, 26.03) * mm});
            skArc(sketch, "E13.31.2", {"start": v(27.09, 27.01) * mm, "mid": v(26.95, 26.94) * mm, "end": v(26.82, 26.84) * mm});
            skArc(sketch, "E13.31.3", {"start": v(27.09, 27.01) * mm, "mid": v(27.9, 27.32) * mm, "end": v(28.75, 27.54) * mm});
            skArc(sketch, "E13.31.4", {"start": v(29.53, 27.3) * mm, "mid": v(29.17, 27.52) * mm, "end": v(28.75, 27.54) * mm});
            skArc(sketch, "E13.31.5", {"start": v(29.53, 27.3) * mm, "mid": v(29.6, 27.23) * mm, "end": v(29.65, 27.17) * mm});
            skArc(sketch, "E13.31.6", {"start": v(29.77, 27.04) * mm, "mid": v(29.7, 27.1) * mm, "end": v(29.65, 27.17) * mm});
            skArc(sketch, "E13.31.7", {"start": v(29.94, 26.24) * mm, "mid": v(29.96, 26.66) * mm, "end": v(29.77, 27.04) * mm});
            skArc(sketch, "E13.31.8", {"start": v(29.27, 24.63) * mm, "mid": v(29.64, 25.42) * mm, "end": v(29.94, 26.24) * mm});
            skArc(sketch, "E13.31.9", {"start": v(29.07, 24.38) * mm, "mid": v(29.18, 24.5) * mm, "end": v(29.27, 24.63) * mm});
            skLineSegment(sketch, "E13.31.10", {"start": v(29.07, 24.38) * mm, "end": v(28.2, 23.65) * mm});
            skArc(sketch, "E13.31.11", {"start": v(28.2, 23.65) * mm, "mid": v(27.9, 23.1) * mm, "end": v(28.08, 22.5) * mm});
            skArc(sketch, "E13.32.0", {"start": v(19.97, 29.94) * mm, "mid": v(20.58, 29.81) * mm, "end": v(21.1, 30.15) * mm});
            skLineSegment(sketch, "E13.32.1", {"start": v(21.76, 31.09) * mm, "end": v(21.1, 30.15) * mm});
            skArc(sketch, "E13.32.2", {"start": v(21.98, 31.3) * mm, "mid": v(21.86, 31.2) * mm, "end": v(21.76, 31.09) * mm});
            skArc(sketch, "E13.32.3", {"start": v(21.98, 31.3) * mm, "mid": v(22.74, 31.75) * mm, "end": v(23.53, 32.12) * mm});
            skArc(sketch, "E13.32.4", {"start": v(24.34, 32.01) * mm, "mid": v(23.95, 32.17) * mm, "end": v(23.53, 32.12) * mm});
            skArc(sketch, "E13.32.5", {"start": v(24.34, 32.01) * mm, "mid": v(24.41, 31.96) * mm, "end": v(24.48, 31.9) * mm});
            skArc(sketch, "E13.32.6", {"start": v(24.62, 31.8) * mm, "mid": v(24.55, 31.85) * mm, "end": v(24.48, 31.9) * mm});
            skArc(sketch, "E13.32.7", {"start": v(24.93, 31.04) * mm, "mid": v(24.88, 31.46) * mm, "end": v(24.62, 31.8) * mm});
            skArc(sketch, "E13.32.8", {"start": v(24.55, 29.34) * mm, "mid": v(24.78, 30.18) * mm, "end": v(24.93, 31.04) * mm});
            skArc(sketch, "E13.32.9", {"start": v(24.4, 29.06) * mm, "mid": v(24.48, 29.2) * mm, "end": v(24.55, 29.34) * mm});
            skLineSegment(sketch, "E13.32.10", {"start": v(24.4, 29.06) * mm, "end": v(23.66, 28.19) * mm});
            skArc(sketch, "E13.32.11", {"start": v(23.66, 28.19) * mm, "mid": v(23.47, 27.6) * mm, "end": v(23.75, 27.03) * mm});
            skArc(sketch, "E13.33.0", {"start": v(14.47, 32.95) * mm, "mid": v(15.09, 32.93) * mm, "end": v(15.55, 33.35) * mm});
            skLineSegment(sketch, "E13.33.1", {"start": v(16.03, 34.4) * mm, "end": v(15.55, 33.35) * mm});
            skArc(sketch, "E13.33.2", {"start": v(16.21, 34.65) * mm, "mid": v(16.1, 34.53) * mm, "end": v(16.03, 34.4) * mm});
            skArc(sketch, "E13.33.3", {"start": v(16.21, 34.65) * mm, "mid": v(16.88, 35.21) * mm, "end": v(17.6, 35.71) * mm});
            skArc(sketch, "E13.33.4", {"start": v(18.42, 35.75) * mm, "mid": v(18, 35.84) * mm, "end": v(17.6, 35.71) * mm});
            skArc(sketch, "E13.33.5", {"start": v(18.42, 35.75) * mm, "mid": v(18.5, 35.71) * mm, "end": v(18.57, 35.67) * mm});
            skArc(sketch, "E13.33.6", {"start": v(18.72, 35.6) * mm, "mid": v(18.65, 35.63) * mm, "end": v(18.57, 35.67) * mm});
            skArc(sketch, "E13.33.7", {"start": v(19.16, 34.9) * mm, "mid": v(19.04, 35.3) * mm, "end": v(18.72, 35.6) * mm});
            skArc(sketch, "E13.33.8", {"start": v(19.08, 33.15) * mm, "mid": v(19.16, 34.02) * mm, "end": v(19.16, 34.9) * mm});
            skArc(sketch, "E13.33.9", {"start": v(18.98, 32.86) * mm, "mid": v(19.04, 33) * mm, "end": v(19.08, 33.15) * mm});
            skLineSegment(sketch, "E13.33.10", {"start": v(18.98, 32.86) * mm, "end": v(18.4, 31.87) * mm});
            skArc(sketch, "E13.33.11", {"start": v(18.4, 31.87) * mm, "mid": v(18.32, 31.25) * mm, "end": v(18.7, 30.75) * mm});
            skArc(sketch, "E13.34.0", {"start": v(8.52, 34.96) * mm, "mid": v(9.14, 35.05) * mm, "end": v(9.52, 35.55) * mm});
            skLineSegment(sketch, "E13.34.1", {"start": v(9.81, 36.65) * mm, "end": v(9.52, 35.55) * mm});
            skArc(sketch, "E13.34.2", {"start": v(9.95, 36.94) * mm, "mid": v(9.87, 36.8) * mm, "end": v(9.81, 36.65) * mm});
            skArc(sketch, "E13.34.3", {"start": v(9.95, 36.94) * mm, "mid": v(10.5, 37.6) * mm, "end": v(11.13, 38.23) * mm});
            skArc(sketch, "E13.34.4", {"start": v(11.93, 38.4) * mm, "mid": v(11.5, 38.42) * mm, "end": v(11.13, 38.23) * mm});
            skArc(sketch, "E13.34.5", {"start": v(11.93, 38.4) * mm, "mid": v(12.01, 38.38) * mm, "end": v(12.1, 38.36) * mm});
            skArc(sketch, "E13.34.6", {"start": v(12.26, 38.3) * mm, "mid": v(12.18, 38.33) * mm, "end": v(12.1, 38.36) * mm});
            skArc(sketch, "E13.34.7", {"start": v(12.81, 37.7) * mm, "mid": v(12.62, 38.07) * mm, "end": v(12.26, 38.3) * mm});
            skArc(sketch, "E13.34.8", {"start": v(13.03, 35.96) * mm, "mid": v(12.96, 36.83) * mm, "end": v(12.81, 37.7) * mm});
            skArc(sketch, "E13.34.9", {"start": v(12.98, 35.65) * mm, "mid": v(13.02, 35.8) * mm, "end": v(13.03, 35.96) * mm});
            skLineSegment(sketch, "E13.34.10", {"start": v(12.98, 35.65) * mm, "end": v(12.6, 34.58) * mm});
            skArc(sketch, "E13.34.11", {"start": v(12.6, 34.58) * mm, "mid": v(12.62, 33.95) * mm, "end": v(13.07, 33.53) * mm});
            skArc(sketch, "E13.35.0", {"start": v(2.32, 35.9) * mm, "mid": v(2.92, 36.1) * mm, "end": v(3.2, 36.66) * mm});
            skLineSegment(sketch, "E13.35.1", {"start": v(3.3, 37.8) * mm, "end": v(3.2, 36.66) * mm});
            skArc(sketch, "E13.35.2", {"start": v(3.39, 38.1) * mm, "mid": v(3.33, 37.96) * mm, "end": v(3.3, 37.8) * mm});
            skArc(sketch, "E13.35.3", {"start": v(3.39, 38.1) * mm, "mid": v(3.82, 38.86) * mm, "end": v(4.32, 39.58) * mm});
            skArc(sketch, "E13.35.4", {"start": v(5.08, 39.9) * mm, "mid": v(4.66, 39.84) * mm, "end": v(4.32, 39.58) * mm});
            skArc(sketch, "E13.35.5", {"start": v(5.08, 39.9) * mm, "mid": v(5.16, 39.88) * mm, "end": v(5.25, 39.87) * mm});
            skArc(sketch, "E13.35.6", {"start": v(5.42, 39.85) * mm, "mid": v(5.34, 39.86) * mm, "end": v(5.25, 39.87) * mm});
            skArc(sketch, "E13.35.7", {"start": v(6.07, 39.35) * mm, "mid": v(5.81, 39.69) * mm, "end": v(5.42, 39.85) * mm});
            skArc(sketch, "E13.35.8", {"start": v(6.6, 37.68) * mm, "mid": v(6.37, 38.53) * mm, "end": v(6.07, 39.35) * mm});
            skArc(sketch, "E13.35.9", {"start": v(6.6, 37.37) * mm, "mid": v(6.6, 37.52) * mm, "end": v(6.6, 37.68) * mm});
            skLineSegment(sketch, "E13.35.10", {"start": v(6.6, 37.37) * mm, "end": v(6.4, 36.24) * mm});
            skArc(sketch, "E13.35.11", {"start": v(6.4, 36.24) * mm, "mid": v(6.53, 35.63) * mm, "end": v(7.05, 35.29) * mm});
            skArc(sketch, "E14.trimOffspring", {"start": v(-10.1, 34.54) * mm, "mid": v(-10.82, 34.32) * mm, "end": v(-11.54, 34.08) * mm});
            skArc(sketch, "E15.trimOffspring", {"start": v(-15.94, 32.26) * mm, "mid": v(-16.62, 31.92) * mm, "end": v(-17.28, 31.56) * mm});
            skArc(sketch, "E16.trimOffspring", {"start": v(-21.3, 29) * mm, "mid": v(-21.9, 28.55) * mm, "end": v(-22.5, 28.08) * mm});
            skArc(sketch, "E17.trimOffspring", {"start": v(-26.01, 24.86) * mm, "mid": v(-26.53, 24.3) * mm, "end": v(-27.03, 23.75) * mm});
            skArc(sketch, "E18.trimOffspring", {"start": v(-29.94, 19.97) * mm, "mid": v(-30.35, 19.33) * mm, "end": v(-30.75, 18.7) * mm});
            skArc(sketch, "E19.trimOffspring", {"start": v(-32.95, 14.47) * mm, "mid": v(-33.24, 13.77) * mm, "end": v(-33.53, 13.07) * mm});
            skArc(sketch, "E20.trimOffspring", {"start": v(2.32, 35.9) * mm, "mid": v(1.57, 35.95) * mm, "end": v(0.81, 35.97) * mm});
            skArc(sketch, "E21.trimOffspring", {"start": v(8.52, 34.96) * mm, "mid": v(7.79, 35.13) * mm, "end": v(7.05, 35.29) * mm});
            skArc(sketch, "E22.trimOffspring", {"start": v(14.47, 32.95) * mm, "mid": v(13.77, 33.24) * mm, "end": v(13.07, 33.53) * mm});
            skArc(sketch, "E23.trimOffspring", {"start": v(19.97, 29.94) * mm, "mid": v(19.33, 30.35) * mm, "end": v(18.7, 30.75) * mm});
            skArc(sketch, "E24.trimOffspring", {"start": v(24.86, 26.01) * mm, "mid": v(24.3, 26.53) * mm, "end": v(23.75, 27.03) * mm});
            skArc(sketch, "E25.trimOffspring", {"start": v(29, 21.3) * mm, "mid": v(28.55, 21.9) * mm, "end": v(28.08, 22.5) * mm});
            skArc(sketch, "E26.trimOffspring", {"start": v(32.26, 15.94) * mm, "mid": v(31.92, 16.62) * mm, "end": v(31.56, 17.28) * mm});
            skArc(sketch, "E27.trimOffspring", {"start": v(34.54, 10.1) * mm, "mid": v(34.32, 10.82) * mm, "end": v(34.08, 11.54) * mm});
            skArc(sketch, "E28.trimOffspring", {"start": v(35.77, 3.95) * mm, "mid": v(35.68, 4.7) * mm, "end": v(35.57, 5.45) * mm});
            skArc(sketch, "E29.trimOffspring", {"start": v(35.9, -2.32) * mm, "mid": v(35.95, -1.57) * mm, "end": v(35.97, -0.81) * mm});
            skArc(sketch, "E30.trimOffspring", {"start": v(34.96, -8.52) * mm, "mid": v(35.13, -7.79) * mm, "end": v(35.29, -7.05) * mm});
            skArc(sketch, "E31.trimOffspring", {"start": v(32.95, -14.47) * mm, "mid": v(33.24, -13.77) * mm, "end": v(33.53, -13.07) * mm});
            skArc(sketch, "E32.trimOffspring", {"start": v(29.94, -19.97) * mm, "mid": v(30.35, -19.33) * mm, "end": v(30.75, -18.7) * mm});
            skArc(sketch, "E33.trimOffspring", {"start": v(26.01, -24.86) * mm, "mid": v(26.53, -24.3) * mm, "end": v(27.03, -23.75) * mm});
            skArc(sketch, "E34.trimOffspring", {"start": v(21.3, -29) * mm, "mid": v(21.9, -28.55) * mm, "end": v(22.5, -28.08) * mm});
            skArc(sketch, "E35.trimOffspring", {"start": v(15.94, -32.26) * mm, "mid": v(16.62, -31.92) * mm, "end": v(17.28, -31.56) * mm});
            skArc(sketch, "E36.trimOffspring", {"start": v(10.1, -34.54) * mm, "mid": v(10.82, -34.32) * mm, "end": v(11.54, -34.08) * mm});
            skArc(sketch, "E37.trimOffspring", {"start": v(3.95, -35.77) * mm, "mid": v(4.7, -35.68) * mm, "end": v(5.45, -35.57) * mm});
            skArc(sketch, "E38.trimOffspring", {"start": v(-2.32, -35.9) * mm, "mid": v(-1.57, -35.95) * mm, "end": v(-0.81, -35.97) * mm});
            skArc(sketch, "E39.trimOffspring", {"start": v(-8.52, -34.96) * mm, "mid": v(-7.79, -35.13) * mm, "end": v(-7.05, -35.29) * mm});
            skArc(sketch, "E40.trimOffspring", {"start": v(-14.47, -32.95) * mm, "mid": v(-13.77, -33.24) * mm, "end": v(-13.07, -33.53) * mm});
            skArc(sketch, "E41.trimOffspring", {"start": v(-19.97, -29.94) * mm, "mid": v(-19.33, -30.35) * mm, "end": v(-18.7, -30.75) * mm});
            skArc(sketch, "E42.trimOffspring", {"start": v(-24.86, -26.01) * mm, "mid": v(-24.3, -26.53) * mm, "end": v(-23.75, -27.03) * mm});
            skArc(sketch, "E43.trimOffspring", {"start": v(-29, -21.3) * mm, "mid": v(-28.55, -21.9) * mm, "end": v(-28.08, -22.5) * mm});
            skArc(sketch, "E44.trimOffspring", {"start": v(-32.26, -15.94) * mm, "mid": v(-31.92, -16.62) * mm, "end": v(-31.56, -17.28) * mm});
            skArc(sketch, "E45.trimOffspring", {"start": v(-34.54, -10.1) * mm, "mid": v(-34.32, -10.82) * mm, "end": v(-34.08, -11.54) * mm});
            skArc(sketch, "E46.trimOffspring", {"start": v(-35.77, -3.95) * mm, "mid": v(-35.68, -4.7) * mm, "end": v(-35.57, -5.45) * mm});
            skArc(sketch, "E47.trimOffspring", {"start": v(-35.9, 2.32) * mm, "mid": v(-35.95, 1.57) * mm, "end": v(-35.97, 0.81) * mm});
            skArc(sketch, "E48.trimOffspring", {"start": v(-34.96, 8.52) * mm, "mid": v(-35.13, 7.79) * mm, "end": v(-35.29, 7.05) * mm});
            skSolve(sketch);
        }
        {
            var Q0;
            Q0 = qSketchRegion(id + "F0", true);
            extrude(context, id + "F1", {"entities" : qUnion([Q0]), "depth" : 12.7 * mm});
        }
        {
            var Q0;
            Q0=makeQuery(id+"F1.opExtrude","CAP_FACE",FACE,{"disambiguationData":[OSD([sQuery(id+"F0.wireOp",EDGE,"E0"),sQuery(id+"F0.wireOp",EDGE,"E1"),sQuery(id+"F0.wireOp",EDGE,"E2.trimOffspring"),sQuery(id+"F0.wireOp",EDGE,"E3"),sQuery(id+"F0.wireOp",EDGE,"E4.MirrorCS"),sQuery(id+"F0.wireOp",EDGE,"E5.MirrorCS"),sQuery(id+"F0.wireOp",EDGE,"E6.MirrorCS"),sQuery(id+"F0.wireOp",EDGE,"E7.filletArc"),sQuery(id+"F0.wireOp",EDGE,"E8.filletArc"),sQuery(id+"F0.wireOp",EDGE,"E9.filletArc"),sQuery(id+"F0.wireOp",EDGE,"E10.filletArc"),sQuery(id+"F0.wireOp",EDGE,"E11.filletArc"),sQuery(id+"F0.wireOp",EDGE,"E12.filletArc"),sQuery(id+"F0.wireOp",EDGE,"E13.1.0"),sQuery(id+"F0.wireOp",EDGE,"E13.1.1"),sQuery(id+"F0.wireOp",EDGE,"E13.1.2"),sQuery(id+"F0.wireOp",EDGE,"E13.1.3"),sQuery(id+"F0.wireOp",EDGE,"E13.1.4"),sQuery(id+"F0.wireOp",EDGE,"E13.1.5"),sQuery(id+"F0.wireOp",EDGE,"E13.1.6"),sQuery(id+"F0.wireOp",EDGE,"E13.1.7"),sQuery(id+"F0.wireOp",EDGE,"E13.1.8"),sQuery(id+"F0.wireOp",EDGE,"E13.1.9"),sQuery(id+"F0.wireOp",EDGE,"E13.1.10"),sQuery(id+"F0.wireOp",EDGE,"E13.1.11"),sQuery(id+"F0.wireOp",EDGE,"E13.2.0"),sQuery(id+"F0.wireOp",EDGE,"E13.2.1"),sQuery(id+"F0.wireOp",EDGE,"E13.2.2"),sQuery(id+"F0.wireOp",EDGE,"E13.2.3"),sQuery(id+"F0.wireOp",EDGE,"E13.2.4"),sQuery(id+"F0.wireOp",EDGE,"E13.2.5"),sQuery(id+"F0.wireOp",EDGE,"E13.2.6"),sQuery(id+"F0.wireOp",EDGE,"E13.2.7"),sQuery(id+"F0.wireOp",EDGE,"E13.2.8"),sQuery(id+"F0.wireOp",EDGE,"E13.2.9"),sQuery(id+"F0.wireOp",EDGE,"E13.2.10"),sQuery(id+"F0.wireOp",EDGE,"E13.2.11"),sQuery(id+"F0.wireOp",EDGE,"E13.3.0"),sQuery(id+"F0.wireOp",EDGE,"E13.3.1"),sQuery(id+"F0.wireOp",EDGE,"E13.3.2"),sQuery(id+"F0.wireOp",EDGE,"E13.3.3"),sQuery(id+"F0.wireOp",EDGE,"E13.3.4"),sQuery(id+"F0.wireOp",EDGE,"E13.3.5"),sQuery(id+"F0.wireOp",EDGE,"E13.3.6"),sQuery(id+"F0.wireOp",EDGE,"E13.3.7"),sQuery(id+"F0.wireOp",EDGE,"E13.3.8"),sQuery(id+"F0.wireOp",EDGE,"E13.3.9"),sQuery(id+"F0.wireOp",EDGE,"E13.3.10"),sQuery(id+"F0.wireOp",EDGE,"E13.3.11"),sQuery(id+"F0.wireOp",EDGE,"E13.4.0"),sQuery(id+"F0.wireOp",EDGE,"E13.4.1"),sQuery(id+"F0.wireOp",EDGE,"E13.4.2"),sQuery(id+"F0.wireOp",EDGE,"E13.4.3"),sQuery(id+"F0.wireOp",EDGE,"E13.4.4"),sQuery(id+"F0.wireOp",EDGE,"E13.4.5"),sQuery(id+"F0.wireOp",EDGE,"E13.4.6"),sQuery(id+"F0.wireOp",EDGE,"E13.4.7"),sQuery(id+"F0.wireOp",EDGE,"E13.4.8"),sQuery(id+"F0.wireOp",EDGE,"E13.4.9"),sQuery(id+"F0.wireOp",EDGE,"E13.4.10"),sQuery(id+"F0.wireOp",EDGE,"E13.4.11"),sQuery(id+"F0.wireOp",EDGE,"E13.5.0"),sQuery(id+"F0.wireOp",EDGE,"E13.5.1"),sQuery(id+"F0.wireOp",EDGE,"E13.5.2"),sQuery(id+"F0.wireOp",EDGE,"E13.5.3"),sQuery(id+"F0.wireOp",EDGE,"E13.5.4"),sQuery(id+"F0.wireOp",EDGE,"E13.5.5"),sQuery(id+"F0.wireOp",EDGE,"E13.5.6"),sQuery(id+"F0.wireOp",EDGE,"E13.5.7"),sQuery(id+"F0.wireOp",EDGE,"E13.5.8"),sQuery(id+"F0.wireOp",EDGE,"E13.5.9"),sQuery(id+"F0.wireOp",EDGE,"E13.5.10"),sQuery(id+"F0.wireOp",EDGE,"E13.5.11"),sQuery(id+"F0.wireOp",EDGE,"E13.6.0"),sQuery(id+"F0.wireOp",EDGE,"E13.6.1"),sQuery(id+"F0.wireOp",EDGE,"E13.6.2"),sQuery(id+"F0.wireOp",EDGE,"E13.6.3"),sQuery(id+"F0.wireOp",EDGE,"E13.6.4"),sQuery(id+"F0.wireOp",EDGE,"E13.6.5"),sQuery(id+"F0.wireOp",EDGE,"E13.6.6"),sQuery(id+"F0.wireOp",EDGE,"E13.6.7"),sQuery(id+"F0.wireOp",EDGE,"E13.6.8"),sQuery(id+"F0.wireOp",EDGE,"E13.6.9"),sQuery(id+"F0.wireOp",EDGE,"E13.6.10"),sQuery(id+"F0.wireOp",EDGE,"E13.6.11"),sQuery(id+"F0.wireOp",EDGE,"E13.7.0"),sQuery(id+"F0.wireOp",EDGE,"E13.7.1"),sQuery(id+"F0.wireOp",EDGE,"E13.7.2"),sQuery(id+"F0.wireOp",EDGE,"E13.7.3"),sQuery(id+"F0.wireOp",EDGE,"E13.7.4"),sQuery(id+"F0.wireOp",EDGE,"E13.7.5"),sQuery(id+"F0.wireOp",EDGE,"E13.7.6"),sQuery(id+"F0.wireOp",EDGE,"E13.7.7"),sQuery(id+"F0.wireOp",EDGE,"E13.7.8"),sQuery(id+"F0.wireOp",EDGE,"E13.7.9"),sQuery(id+"F0.wireOp",EDGE,"E13.7.10"),sQuery(id+"F0.wireOp",EDGE,"E13.7.11"),sQuery(id+"F0.wireOp",EDGE,"E13.8.0"),sQuery(id+"F0.wireOp",EDGE,"E13.8.1"),sQuery(id+"F0.wireOp",EDGE,"E13.8.2"),sQuery(id+"F0.wireOp",EDGE,"E13.8.3"),sQuery(id+"F0.wireOp",EDGE,"E13.8.4"),sQuery(id+"F0.wireOp",EDGE,"E13.8.5"),sQuery(id+"F0.wireOp",EDGE,"E13.8.6"),sQuery(id+"F0.wireOp",EDGE,"E13.8.7"),sQuery(id+"F0.wireOp",EDGE,"E13.8.8"),sQuery(id+"F0.wireOp",EDGE,"E13.8.9"),sQuery(id+"F0.wireOp",EDGE,"E13.8.10"),sQuery(id+"F0.wireOp",EDGE,"E13.8.11"),sQuery(id+"F0.wireOp",EDGE,"E13.9.0"),sQuery(id+"F0.wireOp",EDGE,"E13.9.1"),sQuery(id+"F0.wireOp",EDGE,"E13.9.2"),sQuery(id+"F0.wireOp",EDGE,"E13.9.3"),sQuery(id+"F0.wireOp",EDGE,"E13.9.4"),sQuery(id+"F0.wireOp",EDGE,"E13.9.5"),sQuery(id+"F0.wireOp",EDGE,"E13.9.6"),sQuery(id+"F0.wireOp",EDGE,"E13.9.7"),sQuery(id+"F0.wireOp",EDGE,"E13.9.8"),sQuery(id+"F0.wireOp",EDGE,"E13.9.9"),sQuery(id+"F0.wireOp",EDGE,"E13.9.10"),sQuery(id+"F0.wireOp",EDGE,"E13.9.11"),sQuery(id+"F0.wireOp",EDGE,"E13.10.0"),sQuery(id+"F0.wireOp",EDGE,"E13.10.1"),sQuery(id+"F0.wireOp",EDGE,"E13.10.2"),sQuery(id+"F0.wireOp",EDGE,"E13.10.3"),sQuery(id+"F0.wireOp",EDGE,"E13.10.4"),sQuery(id+"F0.wireOp",EDGE,"E13.10.5"),sQuery(id+"F0.wireOp",EDGE,"E13.10.6"),sQuery(id+"F0.wireOp",EDGE,"E13.10.7"),sQuery(id+"F0.wireOp",EDGE,"E13.10.8"),sQuery(id+"F0.wireOp",EDGE,"E13.10.9"),sQuery(id+"F0.wireOp",EDGE,"E13.10.10"),sQuery(id+"F0.wireOp",EDGE,"E13.10.11"),sQuery(id+"F0.wireOp",EDGE,"E13.11.0"),sQuery(id+"F0.wireOp",EDGE,"E13.11.1"),sQuery(id+"F0.wireOp",EDGE,"E13.11.2"),sQuery(id+"F0.wireOp",EDGE,"E13.11.3"),sQuery(id+"F0.wireOp",EDGE,"E13.11.4"),sQuery(id+"F0.wireOp",EDGE,"E13.11.5"),sQuery(id+"F0.wireOp",EDGE,"E13.11.6"),sQuery(id+"F0.wireOp",EDGE,"E13.11.7"),sQuery(id+"F0.wireOp",EDGE,"E13.11.8"),sQuery(id+"F0.wireOp",EDGE,"E13.11.9"),sQuery(id+"F0.wireOp",EDGE,"E13.11.10"),sQuery(id+"F0.wireOp",EDGE,"E13.11.11"),sQuery(id+"F0.wireOp",EDGE,"E13.12.0"),sQuery(id+"F0.wireOp",EDGE,"E13.12.1"),sQuery(id+"F0.wireOp",EDGE,"E13.12.2"),sQuery(id+"F0.wireOp",EDGE,"E13.12.3"),sQuery(id+"F0.wireOp",EDGE,"E13.12.4"),sQuery(id+"F0.wireOp",EDGE,"E13.12.5"),sQuery(id+"F0.wireOp",EDGE,"E13.12.6"),sQuery(id+"F0.wireOp",EDGE,"E13.12.7"),sQuery(id+"F0.wireOp",EDGE,"E13.12.8"),sQuery(id+"F0.wireOp",EDGE,"E13.12.9"),sQuery(id+"F0.wireOp",EDGE,"E13.12.10"),sQuery(id+"F0.wireOp",EDGE,"E13.12.11"),sQuery(id+"F0.wireOp",EDGE,"E13.13.0"),sQuery(id+"F0.wireOp",EDGE,"E13.13.1"),sQuery(id+"F0.wireOp",EDGE,"E13.13.2"),sQuery(id+"F0.wireOp",EDGE,"E13.13.3"),sQuery(id+"F0.wireOp",EDGE,"E13.13.4"),sQuery(id+"F0.wireOp",EDGE,"E13.13.5"),sQuery(id+"F0.wireOp",EDGE,"E13.13.6"),sQuery(id+"F0.wireOp",EDGE,"E13.13.7"),sQuery(id+"F0.wireOp",EDGE,"E13.13.8"),sQuery(id+"F0.wireOp",EDGE,"E13.13.9"),sQuery(id+"F0.wireOp",EDGE,"E13.13.10"),sQuery(id+"F0.wireOp",EDGE,"E13.13.11"),sQuery(id+"F0.wireOp",EDGE,"E13.14.0"),sQuery(id+"F0.wireOp",EDGE,"E13.14.1"),sQuery(id+"F0.wireOp",EDGE,"E13.14.2"),sQuery(id+"F0.wireOp",EDGE,"E13.14.3"),sQuery(id+"F0.wireOp",EDGE,"E13.14.4"),sQuery(id+"F0.wireOp",EDGE,"E13.14.5"),sQuery(id+"F0.wireOp",EDGE,"E13.14.6"),sQuery(id+"F0.wireOp",EDGE,"E13.14.7"),sQuery(id+"F0.wireOp",EDGE,"E13.14.8"),sQuery(id+"F0.wireOp",EDGE,"E13.14.9"),sQuery(id+"F0.wireOp",EDGE,"E13.14.10"),sQuery(id+"F0.wireOp",EDGE,"E13.14.11"),sQuery(id+"F0.wireOp",EDGE,"E13.15.0"),sQuery(id+"F0.wireOp",EDGE,"E13.15.1"),sQuery(id+"F0.wireOp",EDGE,"E13.15.2"),sQuery(id+"F0.wireOp",EDGE,"E13.15.3"),sQuery(id+"F0.wireOp",EDGE,"E13.15.4"),sQuery(id+"F0.wireOp",EDGE,"E13.15.5"),sQuery(id+"F0.wireOp",EDGE,"E13.15.6"),sQuery(id+"F0.wireOp",EDGE,"E13.15.7"),sQuery(id+"F0.wireOp",EDGE,"E13.15.8"),sQuery(id+"F0.wireOp",EDGE,"E13.15.9"),sQuery(id+"F0.wireOp",EDGE,"E13.15.10"),sQuery(id+"F0.wireOp",EDGE,"E13.15.11"),sQuery(id+"F0.wireOp",EDGE,"E13.16.0"),sQuery(id+"F0.wireOp",EDGE,"E13.16.1"),sQuery(id+"F0.wireOp",EDGE,"E13.16.2"),sQuery(id+"F0.wireOp",EDGE,"E13.16.3"),sQuery(id+"F0.wireOp",EDGE,"E13.16.4"),sQuery(id+"F0.wireOp",EDGE,"E13.16.5"),sQuery(id+"F0.wireOp",EDGE,"E13.16.6"),sQuery(id+"F0.wireOp",EDGE,"E13.16.7"),sQuery(id+"F0.wireOp",EDGE,"E13.16.8"),sQuery(id+"F0.wireOp",EDGE,"E13.16.9"),sQuery(id+"F0.wireOp",EDGE,"E13.16.10"),sQuery(id+"F0.wireOp",EDGE,"E13.16.11"),sQuery(id+"F0.wireOp",EDGE,"E13.17.0"),sQuery(id+"F0.wireOp",EDGE,"E13.17.1"),sQuery(id+"F0.wireOp",EDGE,"E13.17.2"),sQuery(id+"F0.wireOp",EDGE,"E13.17.3"),sQuery(id+"F0.wireOp",EDGE,"E13.17.4"),sQuery(id+"F0.wireOp",EDGE,"E13.17.5"),sQuery(id+"F0.wireOp",EDGE,"E13.17.6"),sQuery(id+"F0.wireOp",EDGE,"E13.17.7"),sQuery(id+"F0.wireOp",EDGE,"E13.17.8"),sQuery(id+"F0.wireOp",EDGE,"E13.17.9"),sQuery(id+"F0.wireOp",EDGE,"E13.17.10"),sQuery(id+"F0.wireOp",EDGE,"E13.17.11"),sQuery(id+"F0.wireOp",EDGE,"E13.18.0"),sQuery(id+"F0.wireOp",EDGE,"E13.18.1"),sQuery(id+"F0.wireOp",EDGE,"E13.18.2"),sQuery(id+"F0.wireOp",EDGE,"E13.18.3"),sQuery(id+"F0.wireOp",EDGE,"E13.18.4"),sQuery(id+"F0.wireOp",EDGE,"E13.18.5"),sQuery(id+"F0.wireOp",EDGE,"E13.18.6"),sQuery(id+"F0.wireOp",EDGE,"E13.18.7"),sQuery(id+"F0.wireOp",EDGE,"E13.18.8"),sQuery(id+"F0.wireOp",EDGE,"E13.18.9"),sQuery(id+"F0.wireOp",EDGE,"E13.18.10"),sQuery(id+"F0.wireOp",EDGE,"E13.18.11"),sQuery(id+"F0.wireOp",EDGE,"E13.19.0"),sQuery(id+"F0.wireOp",EDGE,"E13.19.1"),sQuery(id+"F0.wireOp",EDGE,"E13.19.2"),sQuery(id+"F0.wireOp",EDGE,"E13.19.3"),sQuery(id+"F0.wireOp",EDGE,"E13.19.4"),sQuery(id+"F0.wireOp",EDGE,"E13.19.5"),sQuery(id+"F0.wireOp",EDGE,"E13.19.6"),sQuery(id+"F0.wireOp",EDGE,"E13.19.7"),sQuery(id+"F0.wireOp",EDGE,"E13.19.8"),sQuery(id+"F0.wireOp",EDGE,"E13.19.9"),sQuery(id+"F0.wireOp",EDGE,"E13.19.10"),sQuery(id+"F0.wireOp",EDGE,"E13.19.11"),sQuery(id+"F0.wireOp",EDGE,"E13.20.0"),sQuery(id+"F0.wireOp",EDGE,"E13.20.1"),sQuery(id+"F0.wireOp",EDGE,"E13.20.2"),sQuery(id+"F0.wireOp",EDGE,"E13.20.3"),sQuery(id+"F0.wireOp",EDGE,"E13.20.4"),sQuery(id+"F0.wireOp",EDGE,"E13.20.5"),sQuery(id+"F0.wireOp",EDGE,"E13.20.6"),sQuery(id+"F0.wireOp",EDGE,"E13.20.7"),sQuery(id+"F0.wireOp",EDGE,"E13.20.8"),sQuery(id+"F0.wireOp",EDGE,"E13.20.9"),sQuery(id+"F0.wireOp",EDGE,"E13.20.10"),sQuery(id+"F0.wireOp",EDGE,"E13.20.11"),sQuery(id+"F0.wireOp",EDGE,"E13.21.0"),sQuery(id+"F0.wireOp",EDGE,"E13.21.1"),sQuery(id+"F0.wireOp",EDGE,"E13.21.2"),sQuery(id+"F0.wireOp",EDGE,"E13.21.3"),sQuery(id+"F0.wireOp",EDGE,"E13.21.4"),sQuery(id+"F0.wireOp",EDGE,"E13.21.5"),sQuery(id+"F0.wireOp",EDGE,"E13.21.6"),sQuery(id+"F0.wireOp",EDGE,"E13.21.7"),sQuery(id+"F0.wireOp",EDGE,"E13.21.8"),sQuery(id+"F0.wireOp",EDGE,"E13.21.9"),sQuery(id+"F0.wireOp",EDGE,"E13.21.10"),sQuery(id+"F0.wireOp",EDGE,"E13.21.11"),sQuery(id+"F0.wireOp",EDGE,"E13.22.0"),sQuery(id+"F0.wireOp",EDGE,"E13.22.1"),sQuery(id+"F0.wireOp",EDGE,"E13.22.2"),sQuery(id+"F0.wireOp",EDGE,"E13.22.3"),sQuery(id+"F0.wireOp",EDGE,"E13.22.4"),sQuery(id+"F0.wireOp",EDGE,"E13.22.5"),sQuery(id+"F0.wireOp",EDGE,"E13.22.6"),sQuery(id+"F0.wireOp",EDGE,"E13.22.7"),sQuery(id+"F0.wireOp",EDGE,"E13.22.8"),sQuery(id+"F0.wireOp",EDGE,"E13.22.9"),sQuery(id+"F0.wireOp",EDGE,"E13.22.10"),sQuery(id+"F0.wireOp",EDGE,"E13.22.11"),sQuery(id+"F0.wireOp",EDGE,"E13.23.0"),sQuery(id+"F0.wireOp",EDGE,"E13.23.1"),sQuery(id+"F0.wireOp",EDGE,"E13.23.2"),sQuery(id+"F0.wireOp",EDGE,"E13.23.3"),sQuery(id+"F0.wireOp",EDGE,"E13.23.4"),sQuery(id+"F0.wireOp",EDGE,"E13.23.5"),sQuery(id+"F0.wireOp",EDGE,"E13.23.6"),sQuery(id+"F0.wireOp",EDGE,"E13.23.7"),sQuery(id+"F0.wireOp",EDGE,"E13.23.8"),sQuery(id+"F0.wireOp",EDGE,"E13.23.9"),sQuery(id+"F0.wireOp",EDGE,"E13.23.10"),sQuery(id+"F0.wireOp",EDGE,"E13.23.11"),sQuery(id+"F0.wireOp",EDGE,"E13.24.0"),sQuery(id+"F0.wireOp",EDGE,"E13.24.1"),sQuery(id+"F0.wireOp",EDGE,"E13.24.2"),sQuery(id+"F0.wireOp",EDGE,"E13.24.3"),sQuery(id+"F0.wireOp",EDGE,"E13.24.4"),sQuery(id+"F0.wireOp",EDGE,"E13.24.5"),sQuery(id+"F0.wireOp",EDGE,"E13.24.6"),sQuery(id+"F0.wireOp",EDGE,"E13.24.7"),sQuery(id+"F0.wireOp",EDGE,"E13.24.8"),sQuery(id+"F0.wireOp",EDGE,"E13.24.9"),sQuery(id+"F0.wireOp",EDGE,"E13.24.10"),sQuery(id+"F0.wireOp",EDGE,"E13.24.11"),sQuery(id+"F0.wireOp",EDGE,"E13.25.0"),sQuery(id+"F0.wireOp",EDGE,"E13.25.1"),sQuery(id+"F0.wireOp",EDGE,"E13.25.2"),sQuery(id+"F0.wireOp",EDGE,"E13.25.3"),sQuery(id+"F0.wireOp",EDGE,"E13.25.4"),sQuery(id+"F0.wireOp",EDGE,"E13.25.5"),sQuery(id+"F0.wireOp",EDGE,"E13.25.6"),sQuery(id+"F0.wireOp",EDGE,"E13.25.7"),sQuery(id+"F0.wireOp",EDGE,"E13.25.8"),sQuery(id+"F0.wireOp",EDGE,"E13.25.9"),sQuery(id+"F0.wireOp",EDGE,"E13.25.10"),sQuery(id+"F0.wireOp",EDGE,"E13.25.11"),sQuery(id+"F0.wireOp",EDGE,"E13.26.0"),sQuery(id+"F0.wireOp",EDGE,"E13.26.1"),sQuery(id+"F0.wireOp",EDGE,"E13.26.2"),sQuery(id+"F0.wireOp",EDGE,"E13.26.3"),sQuery(id+"F0.wireOp",EDGE,"E13.26.4"),sQuery(id+"F0.wireOp",EDGE,"E13.26.5"),sQuery(id+"F0.wireOp",EDGE,"E13.26.6"),sQuery(id+"F0.wireOp",EDGE,"E13.26.7"),sQuery(id+"F0.wireOp",EDGE,"E13.26.8"),sQuery(id+"F0.wireOp",EDGE,"E13.26.9"),sQuery(id+"F0.wireOp",EDGE,"E13.26.10"),sQuery(id+"F0.wireOp",EDGE,"E13.26.11"),sQuery(id+"F0.wireOp",EDGE,"E13.27.0"),sQuery(id+"F0.wireOp",EDGE,"E13.27.1"),sQuery(id+"F0.wireOp",EDGE,"E13.27.2"),sQuery(id+"F0.wireOp",EDGE,"E13.27.3"),sQuery(id+"F0.wireOp",EDGE,"E13.27.4"),sQuery(id+"F0.wireOp",EDGE,"E13.27.5"),sQuery(id+"F0.wireOp",EDGE,"E13.27.6"),sQuery(id+"F0.wireOp",EDGE,"E13.27.7"),sQuery(id+"F0.wireOp",EDGE,"E13.27.8"),sQuery(id+"F0.wireOp",EDGE,"E13.27.9"),sQuery(id+"F0.wireOp",EDGE,"E13.27.10"),sQuery(id+"F0.wireOp",EDGE,"E13.27.11"),sQuery(id+"F0.wireOp",EDGE,"E13.28.0"),sQuery(id+"F0.wireOp",EDGE,"E13.28.1"),sQuery(id+"F0.wireOp",EDGE,"E13.28.2"),sQuery(id+"F0.wireOp",EDGE,"E13.28.3"),sQuery(id+"F0.wireOp",EDGE,"E13.28.4"),sQuery(id+"F0.wireOp",EDGE,"E13.28.5"),sQuery(id+"F0.wireOp",EDGE,"E13.28.6"),sQuery(id+"F0.wireOp",EDGE,"E13.28.7"),sQuery(id+"F0.wireOp",EDGE,"E13.28.8"),sQuery(id+"F0.wireOp",EDGE,"E13.28.9"),sQuery(id+"F0.wireOp",EDGE,"E13.28.10"),sQuery(id+"F0.wireOp",EDGE,"E13.28.11"),sQuery(id+"F0.wireOp",EDGE,"E13.29.0"),sQuery(id+"F0.wireOp",EDGE,"E13.29.1"),sQuery(id+"F0.wireOp",EDGE,"E13.29.2"),sQuery(id+"F0.wireOp",EDGE,"E13.29.3"),sQuery(id+"F0.wireOp",EDGE,"E13.29.4"),sQuery(id+"F0.wireOp",EDGE,"E13.29.5"),sQuery(id+"F0.wireOp",EDGE,"E13.29.6"),sQuery(id+"F0.wireOp",EDGE,"E13.29.7"),sQuery(id+"F0.wireOp",EDGE,"E13.29.8"),sQuery(id+"F0.wireOp",EDGE,"E13.29.9"),sQuery(id+"F0.wireOp",EDGE,"E13.29.10"),sQuery(id+"F0.wireOp",EDGE,"E13.29.11"),sQuery(id+"F0.wireOp",EDGE,"E13.30.0"),sQuery(id+"F0.wireOp",EDGE,"E13.30.1"),sQuery(id+"F0.wireOp",EDGE,"E13.30.2"),sQuery(id+"F0.wireOp",EDGE,"E13.30.3"),sQuery(id+"F0.wireOp",EDGE,"E13.30.4"),sQuery(id+"F0.wireOp",EDGE,"E13.30.5"),sQuery(id+"F0.wireOp",EDGE,"E13.30.6"),sQuery(id+"F0.wireOp",EDGE,"E13.30.7"),sQuery(id+"F0.wireOp",EDGE,"E13.30.8"),sQuery(id+"F0.wireOp",EDGE,"E13.30.9"),sQuery(id+"F0.wireOp",EDGE,"E13.30.10"),sQuery(id+"F0.wireOp",EDGE,"E13.30.11"),sQuery(id+"F0.wireOp",EDGE,"E13.31.0"),sQuery(id+"F0.wireOp",EDGE,"E13.31.1"),sQuery(id+"F0.wireOp",EDGE,"E13.31.2"),sQuery(id+"F0.wireOp",EDGE,"E13.31.3"),sQuery(id+"F0.wireOp",EDGE,"E13.31.4"),sQuery(id+"F0.wireOp",EDGE,"E13.31.5"),sQuery(id+"F0.wireOp",EDGE,"E13.31.6"),sQuery(id+"F0.wireOp",EDGE,"E13.31.7"),sQuery(id+"F0.wireOp",EDGE,"E13.31.8"),sQuery(id+"F0.wireOp",EDGE,"E13.31.9"),sQuery(id+"F0.wireOp",EDGE,"E13.31.10"),sQuery(id+"F0.wireOp",EDGE,"E13.31.11"),sQuery(id+"F0.wireOp",EDGE,"E13.32.0"),sQuery(id+"F0.wireOp",EDGE,"E13.32.1"),sQuery(id+"F0.wireOp",EDGE,"E13.32.2"),sQuery(id+"F0.wireOp",EDGE,"E13.32.3"),sQuery(id+"F0.wireOp",EDGE,"E13.32.4"),sQuery(id+"F0.wireOp",EDGE,"E13.32.5"),sQuery(id+"F0.wireOp",EDGE,"E13.32.6"),sQuery(id+"F0.wireOp",EDGE,"E13.32.7"),sQuery(id+"F0.wireOp",EDGE,"E13.32.8"),sQuery(id+"F0.wireOp",EDGE,"E13.32.9"),sQuery(id+"F0.wireOp",EDGE,"E13.32.10"),sQuery(id+"F0.wireOp",EDGE,"E13.32.11"),sQuery(id+"F0.wireOp",EDGE,"E13.33.0"),sQuery(id+"F0.wireOp",EDGE,"E13.33.1"),sQuery(id+"F0.wireOp",EDGE,"E13.33.2"),sQuery(id+"F0.wireOp",EDGE,"E13.33.3"),sQuery(id+"F0.wireOp",EDGE,"E13.33.4"),sQuery(id+"F0.wireOp",EDGE,"E13.33.5"),sQuery(id+"F0.wireOp",EDGE,"E13.33.6"),sQuery(id+"F0.wireOp",EDGE,"E13.33.7"),sQuery(id+"F0.wireOp",EDGE,"E13.33.8"),sQuery(id+"F0.wireOp",EDGE,"E13.33.9"),sQuery(id+"F0.wireOp",EDGE,"E13.33.10"),sQuery(id+"F0.wireOp",EDGE,"E13.33.11"),sQuery(id+"F0.wireOp",EDGE,"E13.34.0"),sQuery(id+"F0.wireOp",EDGE,"E13.34.1"),sQuery(id+"F0.wireOp",EDGE,"E13.34.2"),sQuery(id+"F0.wireOp",EDGE,"E13.34.3"),sQuery(id+"F0.wireOp",EDGE,"E13.34.4"),sQuery(id+"F0.wireOp",EDGE,"E13.34.5"),sQuery(id+"F0.wireOp",EDGE,"E13.34.6"),sQuery(id+"F0.wireOp",EDGE,"E13.34.7"),sQuery(id+"F0.wireOp",EDGE,"E13.34.8"),sQuery(id+"F0.wireOp",EDGE,"E13.34.9"),sQuery(id+"F0.wireOp",EDGE,"E13.34.10"),sQuery(id+"F0.wireOp",EDGE,"E13.34.11"),sQuery(id+"F0.wireOp",EDGE,"E13.35.0"),sQuery(id+"F0.wireOp",EDGE,"E13.35.1"),sQuery(id+"F0.wireOp",EDGE,"E13.35.2"),sQuery(id+"F0.wireOp",EDGE,"E13.35.3"),sQuery(id+"F0.wireOp",EDGE,"E13.35.4"),sQuery(id+"F0.wireOp",EDGE,"E13.35.5"),sQuery(id+"F0.wireOp",EDGE,"E13.35.6"),sQuery(id+"F0.wireOp",EDGE,"E13.35.7"),sQuery(id+"F0.wireOp",EDGE,"E13.35.8"),sQuery(id+"F0.wireOp",EDGE,"E13.35.9"),sQuery(id+"F0.wireOp",EDGE,"E13.35.10"),sQuery(id+"F0.wireOp",EDGE,"E13.35.11"),sQuery(id+"F0.wireOp",EDGE,"E14.trimOffspring"),sQuery(id+"F0.wireOp",EDGE,"E15.trimOffspring"),sQuery(id+"F0.wireOp",EDGE,"E16.trimOffspring"),sQuery(id+"F0.wireOp",EDGE,"E17.trimOffspring"),sQuery(id+"F0.wireOp",EDGE,"E18.trimOffspring"),sQuery(id+"F0.wireOp",EDGE,"E19.trimOffspring"),sQuery(id+"F0.wireOp",EDGE,"E20.trimOffspring"),sQuery(id+"F0.wireOp",EDGE,"E21.trimOffspring"),sQuery(id+"F0.wireOp",EDGE,"E22.trimOffspring"),sQuery(id+"F0.wireOp",EDGE,"E23.trimOffspring"),sQuery(id+"F0.wireOp",EDGE,"E24.trimOffspring"),sQuery(id+"F0.wireOp",EDGE,"E25.trimOffspring"),sQuery(id+"F0.wireOp",EDGE,"E26.trimOffspring"),sQuery(id+"F0.wireOp",EDGE,"E27.trimOffspring"),sQuery(id+"F0.wireOp",EDGE,"E28.trimOffspring"),sQuery(id+"F0.wireOp",EDGE,"E29.trimOffspring"),sQuery(id+"F0.wireOp",EDGE,"E30.trimOffspring"),sQuery(id+"F0.wireOp",EDGE,"E31.trimOffspring"),sQuery(id+"F0.wireOp",EDGE,"E32.trimOffspring"),sQuery(id+"F0.wireOp",EDGE,"E33.trimOffspring"),sQuery(id+"F0.wireOp",EDGE,"E34.trimOffspring"),sQuery(id+"F0.wireOp",EDGE,"E35.trimOffspring"),sQuery(id+"F0.wireOp",EDGE,"E36.trimOffspring"),sQuery(id+"F0.wireOp",EDGE,"E37.trimOffspring"),sQuery(id+"F0.wireOp",EDGE,"E38.trimOffspring"),sQuery(id+"F0.wireOp",EDGE,"E39.trimOffspring"),sQuery(id+"F0.wireOp",EDGE,"E40.trimOffspring"),sQuery(id+"F0.wireOp",EDGE,"E41.trimOffspring"),sQuery(id+"F0.wireOp",EDGE,"E42.trimOffspring"),sQuery(id+"F0.wireOp",EDGE,"E43.trimOffspring"),sQuery(id+"F0.wireOp",EDGE,"E44.trimOffspring"),sQuery(id+"F0.wireOp",EDGE,"E45.trimOffspring"),sQuery(id+"F0.wireOp",EDGE,"E46.trimOffspring"),sQuery(id+"F0.wireOp",EDGE,"E47.trimOffspring"),sQuery(id+"F0.wireOp",EDGE,"E48.trimOffspring")])],"isStart":false});
            var sketch = newSketch(context, id + "F2", { "sketchPlane" : qUnion([Q0])});
            skCircle(sketch, "E49", {"center": v(0, 0) * mm, "radius": 3.18 * mm});
            skSolve(sketch);
        }
        {
            var Q0;
            Q0 = qSketchRegion(id + "F2", true);
            extrude(context, id + "F3", {"entities" : qUnion([Q0]), "operationType" : NewBodyOperationType.REMOVE, "endBound" : BoundingType.THROUGH_ALL, "oppositeDirection" : true, "depth" : 25.4 * mm});
        }
        {
            var Q0;
            Q0=makeQuery(id+"F1.opExtrude","CAP_FACE",FACE,{"disambiguationData":[OSD([sQuery(id+"F0.wireOp",EDGE,"E0"),sQuery(id+"F0.wireOp",EDGE,"E1"),sQuery(id+"F0.wireOp",EDGE,"E2.trimOffspring"),sQuery(id+"F0.wireOp",EDGE,"E3"),sQuery(id+"F0.wireOp",EDGE,"E4.MirrorCS"),sQuery(id+"F0.wireOp",EDGE,"E5.MirrorCS"),sQuery(id+"F0.wireOp",EDGE,"E6.MirrorCS"),sQuery(id+"F0.wireOp",EDGE,"E7.filletArc"),sQuery(id+"F0.wireOp",EDGE,"E8.filletArc"),sQuery(id+"F0.wireOp",EDGE,"E9.filletArc"),sQuery(id+"F0.wireOp",EDGE,"E10.filletArc"),sQuery(id+"F0.wireOp",EDGE,"E11.filletArc"),sQuery(id+"F0.wireOp",EDGE,"E12.filletArc"),sQuery(id+"F0.wireOp",EDGE,"E13.1.0"),sQuery(id+"F0.wireOp",EDGE,"E13.1.1"),sQuery(id+"F0.wireOp",EDGE,"E13.1.2"),sQuery(id+"F0.wireOp",EDGE,"E13.1.3"),sQuery(id+"F0.wireOp",EDGE,"E13.1.4"),sQuery(id+"F0.wireOp",EDGE,"E13.1.5"),sQuery(id+"F0.wireOp",EDGE,"E13.1.6"),sQuery(id+"F0.wireOp",EDGE,"E13.1.7"),sQuery(id+"F0.wireOp",EDGE,"E13.1.8"),sQuery(id+"F0.wireOp",EDGE,"E13.1.9"),sQuery(id+"F0.wireOp",EDGE,"E13.1.10"),sQuery(id+"F0.wireOp",EDGE,"E13.1.11"),sQuery(id+"F0.wireOp",EDGE,"E13.2.0"),sQuery(id+"F0.wireOp",EDGE,"E13.2.1"),sQuery(id+"F0.wireOp",EDGE,"E13.2.2"),sQuery(id+"F0.wireOp",EDGE,"E13.2.3"),sQuery(id+"F0.wireOp",EDGE,"E13.2.4"),sQuery(id+"F0.wireOp",EDGE,"E13.2.5"),sQuery(id+"F0.wireOp",EDGE,"E13.2.6"),sQuery(id+"F0.wireOp",EDGE,"E13.2.7"),sQuery(id+"F0.wireOp",EDGE,"E13.2.8"),sQuery(id+"F0.wireOp",EDGE,"E13.2.9"),sQuery(id+"F0.wireOp",EDGE,"E13.2.10"),sQuery(id+"F0.wireOp",EDGE,"E13.2.11"),sQuery(id+"F0.wireOp",EDGE,"E13.3.0"),sQuery(id+"F0.wireOp",EDGE,"E13.3.1"),sQuery(id+"F0.wireOp",EDGE,"E13.3.2"),sQuery(id+"F0.wireOp",EDGE,"E13.3.3"),sQuery(id+"F0.wireOp",EDGE,"E13.3.4"),sQuery(id+"F0.wireOp",EDGE,"E13.3.5"),sQuery(id+"F0.wireOp",EDGE,"E13.3.6"),sQuery(id+"F0.wireOp",EDGE,"E13.3.7"),sQuery(id+"F0.wireOp",EDGE,"E13.3.8"),sQuery(id+"F0.wireOp",EDGE,"E13.3.9"),sQuery(id+"F0.wireOp",EDGE,"E13.3.10"),sQuery(id+"F0.wireOp",EDGE,"E13.3.11"),sQuery(id+"F0.wireOp",EDGE,"E13.4.0"),sQuery(id+"F0.wireOp",EDGE,"E13.4.1"),sQuery(id+"F0.wireOp",EDGE,"E13.4.2"),sQuery(id+"F0.wireOp",EDGE,"E13.4.3"),sQuery(id+"F0.wireOp",EDGE,"E13.4.4"),sQuery(id+"F0.wireOp",EDGE,"E13.4.5"),sQuery(id+"F0.wireOp",EDGE,"E13.4.6"),sQuery(id+"F0.wireOp",EDGE,"E13.4.7"),sQuery(id+"F0.wireOp",EDGE,"E13.4.8"),sQuery(id+"F0.wireOp",EDGE,"E13.4.9"),sQuery(id+"F0.wireOp",EDGE,"E13.4.10"),sQuery(id+"F0.wireOp",EDGE,"E13.4.11"),sQuery(id+"F0.wireOp",EDGE,"E13.5.0"),sQuery(id+"F0.wireOp",EDGE,"E13.5.1"),sQuery(id+"F0.wireOp",EDGE,"E13.5.2"),sQuery(id+"F0.wireOp",EDGE,"E13.5.3"),sQuery(id+"F0.wireOp",EDGE,"E13.5.4"),sQuery(id+"F0.wireOp",EDGE,"E13.5.5"),sQuery(id+"F0.wireOp",EDGE,"E13.5.6"),sQuery(id+"F0.wireOp",EDGE,"E13.5.7"),sQuery(id+"F0.wireOp",EDGE,"E13.5.8"),sQuery(id+"F0.wireOp",EDGE,"E13.5.9"),sQuery(id+"F0.wireOp",EDGE,"E13.5.10"),sQuery(id+"F0.wireOp",EDGE,"E13.5.11"),sQuery(id+"F0.wireOp",EDGE,"E13.6.0"),sQuery(id+"F0.wireOp",EDGE,"E13.6.1"),sQuery(id+"F0.wireOp",EDGE,"E13.6.2"),sQuery(id+"F0.wireOp",EDGE,"E13.6.3"),sQuery(id+"F0.wireOp",EDGE,"E13.6.4"),sQuery(id+"F0.wireOp",EDGE,"E13.6.5"),sQuery(id+"F0.wireOp",EDGE,"E13.6.6"),sQuery(id+"F0.wireOp",EDGE,"E13.6.7"),sQuery(id+"F0.wireOp",EDGE,"E13.6.8"),sQuery(id+"F0.wireOp",EDGE,"E13.6.9"),sQuery(id+"F0.wireOp",EDGE,"E13.6.10"),sQuery(id+"F0.wireOp",EDGE,"E13.6.11"),sQuery(id+"F0.wireOp",EDGE,"E13.7.0"),sQuery(id+"F0.wireOp",EDGE,"E13.7.1"),sQuery(id+"F0.wireOp",EDGE,"E13.7.2"),sQuery(id+"F0.wireOp",EDGE,"E13.7.3"),sQuery(id+"F0.wireOp",EDGE,"E13.7.4"),sQuery(id+"F0.wireOp",EDGE,"E13.7.5"),sQuery(id+"F0.wireOp",EDGE,"E13.7.6"),sQuery(id+"F0.wireOp",EDGE,"E13.7.7"),sQuery(id+"F0.wireOp",EDGE,"E13.7.8"),sQuery(id+"F0.wireOp",EDGE,"E13.7.9"),sQuery(id+"F0.wireOp",EDGE,"E13.7.10"),sQuery(id+"F0.wireOp",EDGE,"E13.7.11"),sQuery(id+"F0.wireOp",EDGE,"E13.8.0"),sQuery(id+"F0.wireOp",EDGE,"E13.8.1"),sQuery(id+"F0.wireOp",EDGE,"E13.8.2"),sQuery(id+"F0.wireOp",EDGE,"E13.8.3"),sQuery(id+"F0.wireOp",EDGE,"E13.8.4"),sQuery(id+"F0.wireOp",EDGE,"E13.8.5"),sQuery(id+"F0.wireOp",EDGE,"E13.8.6"),sQuery(id+"F0.wireOp",EDGE,"E13.8.7"),sQuery(id+"F0.wireOp",EDGE,"E13.8.8"),sQuery(id+"F0.wireOp",EDGE,"E13.8.9"),sQuery(id+"F0.wireOp",EDGE,"E13.8.10"),sQuery(id+"F0.wireOp",EDGE,"E13.8.11"),sQuery(id+"F0.wireOp",EDGE,"E13.9.0"),sQuery(id+"F0.wireOp",EDGE,"E13.9.1"),sQuery(id+"F0.wireOp",EDGE,"E13.9.2"),sQuery(id+"F0.wireOp",EDGE,"E13.9.3"),sQuery(id+"F0.wireOp",EDGE,"E13.9.4"),sQuery(id+"F0.wireOp",EDGE,"E13.9.5"),sQuery(id+"F0.wireOp",EDGE,"E13.9.6"),sQuery(id+"F0.wireOp",EDGE,"E13.9.7"),sQuery(id+"F0.wireOp",EDGE,"E13.9.8"),sQuery(id+"F0.wireOp",EDGE,"E13.9.9"),sQuery(id+"F0.wireOp",EDGE,"E13.9.10"),sQuery(id+"F0.wireOp",EDGE,"E13.9.11"),sQuery(id+"F0.wireOp",EDGE,"E13.10.0"),sQuery(id+"F0.wireOp",EDGE,"E13.10.1"),sQuery(id+"F0.wireOp",EDGE,"E13.10.2"),sQuery(id+"F0.wireOp",EDGE,"E13.10.3"),sQuery(id+"F0.wireOp",EDGE,"E13.10.4"),sQuery(id+"F0.wireOp",EDGE,"E13.10.5"),sQuery(id+"F0.wireOp",EDGE,"E13.10.6"),sQuery(id+"F0.wireOp",EDGE,"E13.10.7"),sQuery(id+"F0.wireOp",EDGE,"E13.10.8"),sQuery(id+"F0.wireOp",EDGE,"E13.10.9"),sQuery(id+"F0.wireOp",EDGE,"E13.10.10"),sQuery(id+"F0.wireOp",EDGE,"E13.10.11"),sQuery(id+"F0.wireOp",EDGE,"E13.11.0"),sQuery(id+"F0.wireOp",EDGE,"E13.11.1"),sQuery(id+"F0.wireOp",EDGE,"E13.11.2"),sQuery(id+"F0.wireOp",EDGE,"E13.11.3"),sQuery(id+"F0.wireOp",EDGE,"E13.11.4"),sQuery(id+"F0.wireOp",EDGE,"E13.11.5"),sQuery(id+"F0.wireOp",EDGE,"E13.11.6"),sQuery(id+"F0.wireOp",EDGE,"E13.11.7"),sQuery(id+"F0.wireOp",EDGE,"E13.11.8"),sQuery(id+"F0.wireOp",EDGE,"E13.11.9"),sQuery(id+"F0.wireOp",EDGE,"E13.11.10"),sQuery(id+"F0.wireOp",EDGE,"E13.11.11"),sQuery(id+"F0.wireOp",EDGE,"E13.12.0"),sQuery(id+"F0.wireOp",EDGE,"E13.12.1"),sQuery(id+"F0.wireOp",EDGE,"E13.12.2"),sQuery(id+"F0.wireOp",EDGE,"E13.12.3"),sQuery(id+"F0.wireOp",EDGE,"E13.12.4"),sQuery(id+"F0.wireOp",EDGE,"E13.12.5"),sQuery(id+"F0.wireOp",EDGE,"E13.12.6"),sQuery(id+"F0.wireOp",EDGE,"E13.12.7"),sQuery(id+"F0.wireOp",EDGE,"E13.12.8"),sQuery(id+"F0.wireOp",EDGE,"E13.12.9"),sQuery(id+"F0.wireOp",EDGE,"E13.12.10"),sQuery(id+"F0.wireOp",EDGE,"E13.12.11"),sQuery(id+"F0.wireOp",EDGE,"E13.13.0"),sQuery(id+"F0.wireOp",EDGE,"E13.13.1"),sQuery(id+"F0.wireOp",EDGE,"E13.13.2"),sQuery(id+"F0.wireOp",EDGE,"E13.13.3"),sQuery(id+"F0.wireOp",EDGE,"E13.13.4"),sQuery(id+"F0.wireOp",EDGE,"E13.13.5"),sQuery(id+"F0.wireOp",EDGE,"E13.13.6"),sQuery(id+"F0.wireOp",EDGE,"E13.13.7"),sQuery(id+"F0.wireOp",EDGE,"E13.13.8"),sQuery(id+"F0.wireOp",EDGE,"E13.13.9"),sQuery(id+"F0.wireOp",EDGE,"E13.13.10"),sQuery(id+"F0.wireOp",EDGE,"E13.13.11"),sQuery(id+"F0.wireOp",EDGE,"E13.14.0"),sQuery(id+"F0.wireOp",EDGE,"E13.14.1"),sQuery(id+"F0.wireOp",EDGE,"E13.14.2"),sQuery(id+"F0.wireOp",EDGE,"E13.14.3"),sQuery(id+"F0.wireOp",EDGE,"E13.14.4"),sQuery(id+"F0.wireOp",EDGE,"E13.14.5"),sQuery(id+"F0.wireOp",EDGE,"E13.14.6"),sQuery(id+"F0.wireOp",EDGE,"E13.14.7"),sQuery(id+"F0.wireOp",EDGE,"E13.14.8"),sQuery(id+"F0.wireOp",EDGE,"E13.14.9"),sQuery(id+"F0.wireOp",EDGE,"E13.14.10"),sQuery(id+"F0.wireOp",EDGE,"E13.14.11"),sQuery(id+"F0.wireOp",EDGE,"E13.15.0"),sQuery(id+"F0.wireOp",EDGE,"E13.15.1"),sQuery(id+"F0.wireOp",EDGE,"E13.15.2"),sQuery(id+"F0.wireOp",EDGE,"E13.15.3"),sQuery(id+"F0.wireOp",EDGE,"E13.15.4"),sQuery(id+"F0.wireOp",EDGE,"E13.15.5"),sQuery(id+"F0.wireOp",EDGE,"E13.15.6"),sQuery(id+"F0.wireOp",EDGE,"E13.15.7"),sQuery(id+"F0.wireOp",EDGE,"E13.15.8"),sQuery(id+"F0.wireOp",EDGE,"E13.15.9"),sQuery(id+"F0.wireOp",EDGE,"E13.15.10"),sQuery(id+"F0.wireOp",EDGE,"E13.15.11"),sQuery(id+"F0.wireOp",EDGE,"E13.16.0"),sQuery(id+"F0.wireOp",EDGE,"E13.16.1"),sQuery(id+"F0.wireOp",EDGE,"E13.16.2"),sQuery(id+"F0.wireOp",EDGE,"E13.16.3"),sQuery(id+"F0.wireOp",EDGE,"E13.16.4"),sQuery(id+"F0.wireOp",EDGE,"E13.16.5"),sQuery(id+"F0.wireOp",EDGE,"E13.16.6"),sQuery(id+"F0.wireOp",EDGE,"E13.16.7"),sQuery(id+"F0.wireOp",EDGE,"E13.16.8"),sQuery(id+"F0.wireOp",EDGE,"E13.16.9"),sQuery(id+"F0.wireOp",EDGE,"E13.16.10"),sQuery(id+"F0.wireOp",EDGE,"E13.16.11"),sQuery(id+"F0.wireOp",EDGE,"E13.17.0"),sQuery(id+"F0.wireOp",EDGE,"E13.17.1"),sQuery(id+"F0.wireOp",EDGE,"E13.17.2"),sQuery(id+"F0.wireOp",EDGE,"E13.17.3"),sQuery(id+"F0.wireOp",EDGE,"E13.17.4"),sQuery(id+"F0.wireOp",EDGE,"E13.17.5"),sQuery(id+"F0.wireOp",EDGE,"E13.17.6"),sQuery(id+"F0.wireOp",EDGE,"E13.17.7"),sQuery(id+"F0.wireOp",EDGE,"E13.17.8"),sQuery(id+"F0.wireOp",EDGE,"E13.17.9"),sQuery(id+"F0.wireOp",EDGE,"E13.17.10"),sQuery(id+"F0.wireOp",EDGE,"E13.17.11"),sQuery(id+"F0.wireOp",EDGE,"E13.18.0"),sQuery(id+"F0.wireOp",EDGE,"E13.18.1"),sQuery(id+"F0.wireOp",EDGE,"E13.18.2"),sQuery(id+"F0.wireOp",EDGE,"E13.18.3"),sQuery(id+"F0.wireOp",EDGE,"E13.18.4"),sQuery(id+"F0.wireOp",EDGE,"E13.18.5"),sQuery(id+"F0.wireOp",EDGE,"E13.18.6"),sQuery(id+"F0.wireOp",EDGE,"E13.18.7"),sQuery(id+"F0.wireOp",EDGE,"E13.18.8"),sQuery(id+"F0.wireOp",EDGE,"E13.18.9"),sQuery(id+"F0.wireOp",EDGE,"E13.18.10"),sQuery(id+"F0.wireOp",EDGE,"E13.18.11"),sQuery(id+"F0.wireOp",EDGE,"E13.19.0"),sQuery(id+"F0.wireOp",EDGE,"E13.19.1"),sQuery(id+"F0.wireOp",EDGE,"E13.19.2"),sQuery(id+"F0.wireOp",EDGE,"E13.19.3"),sQuery(id+"F0.wireOp",EDGE,"E13.19.4"),sQuery(id+"F0.wireOp",EDGE,"E13.19.5"),sQuery(id+"F0.wireOp",EDGE,"E13.19.6"),sQuery(id+"F0.wireOp",EDGE,"E13.19.7"),sQuery(id+"F0.wireOp",EDGE,"E13.19.8"),sQuery(id+"F0.wireOp",EDGE,"E13.19.9"),sQuery(id+"F0.wireOp",EDGE,"E13.19.10"),sQuery(id+"F0.wireOp",EDGE,"E13.19.11"),sQuery(id+"F0.wireOp",EDGE,"E13.20.0"),sQuery(id+"F0.wireOp",EDGE,"E13.20.1"),sQuery(id+"F0.wireOp",EDGE,"E13.20.2"),sQuery(id+"F0.wireOp",EDGE,"E13.20.3"),sQuery(id+"F0.wireOp",EDGE,"E13.20.4"),sQuery(id+"F0.wireOp",EDGE,"E13.20.5"),sQuery(id+"F0.wireOp",EDGE,"E13.20.6"),sQuery(id+"F0.wireOp",EDGE,"E13.20.7"),sQuery(id+"F0.wireOp",EDGE,"E13.20.8"),sQuery(id+"F0.wireOp",EDGE,"E13.20.9"),sQuery(id+"F0.wireOp",EDGE,"E13.20.10"),sQuery(id+"F0.wireOp",EDGE,"E13.20.11"),sQuery(id+"F0.wireOp",EDGE,"E13.21.0"),sQuery(id+"F0.wireOp",EDGE,"E13.21.1"),sQuery(id+"F0.wireOp",EDGE,"E13.21.2"),sQuery(id+"F0.wireOp",EDGE,"E13.21.3"),sQuery(id+"F0.wireOp",EDGE,"E13.21.4"),sQuery(id+"F0.wireOp",EDGE,"E13.21.5"),sQuery(id+"F0.wireOp",EDGE,"E13.21.6"),sQuery(id+"F0.wireOp",EDGE,"E13.21.7"),sQuery(id+"F0.wireOp",EDGE,"E13.21.8"),sQuery(id+"F0.wireOp",EDGE,"E13.21.9"),sQuery(id+"F0.wireOp",EDGE,"E13.21.10"),sQuery(id+"F0.wireOp",EDGE,"E13.21.11"),sQuery(id+"F0.wireOp",EDGE,"E13.22.0"),sQuery(id+"F0.wireOp",EDGE,"E13.22.1"),sQuery(id+"F0.wireOp",EDGE,"E13.22.2"),sQuery(id+"F0.wireOp",EDGE,"E13.22.3"),sQuery(id+"F0.wireOp",EDGE,"E13.22.4"),sQuery(id+"F0.wireOp",EDGE,"E13.22.5"),sQuery(id+"F0.wireOp",EDGE,"E13.22.6"),sQuery(id+"F0.wireOp",EDGE,"E13.22.7"),sQuery(id+"F0.wireOp",EDGE,"E13.22.8"),sQuery(id+"F0.wireOp",EDGE,"E13.22.9"),sQuery(id+"F0.wireOp",EDGE,"E13.22.10"),sQuery(id+"F0.wireOp",EDGE,"E13.22.11"),sQuery(id+"F0.wireOp",EDGE,"E13.23.0"),sQuery(id+"F0.wireOp",EDGE,"E13.23.1"),sQuery(id+"F0.wireOp",EDGE,"E13.23.2"),sQuery(id+"F0.wireOp",EDGE,"E13.23.3"),sQuery(id+"F0.wireOp",EDGE,"E13.23.4"),sQuery(id+"F0.wireOp",EDGE,"E13.23.5"),sQuery(id+"F0.wireOp",EDGE,"E13.23.6"),sQuery(id+"F0.wireOp",EDGE,"E13.23.7"),sQuery(id+"F0.wireOp",EDGE,"E13.23.8"),sQuery(id+"F0.wireOp",EDGE,"E13.23.9"),sQuery(id+"F0.wireOp",EDGE,"E13.23.10"),sQuery(id+"F0.wireOp",EDGE,"E13.23.11"),sQuery(id+"F0.wireOp",EDGE,"E13.24.0"),sQuery(id+"F0.wireOp",EDGE,"E13.24.1"),sQuery(id+"F0.wireOp",EDGE,"E13.24.2"),sQuery(id+"F0.wireOp",EDGE,"E13.24.3"),sQuery(id+"F0.wireOp",EDGE,"E13.24.4"),sQuery(id+"F0.wireOp",EDGE,"E13.24.5"),sQuery(id+"F0.wireOp",EDGE,"E13.24.6"),sQuery(id+"F0.wireOp",EDGE,"E13.24.7"),sQuery(id+"F0.wireOp",EDGE,"E13.24.8"),sQuery(id+"F0.wireOp",EDGE,"E13.24.9"),sQuery(id+"F0.wireOp",EDGE,"E13.24.10"),sQuery(id+"F0.wireOp",EDGE,"E13.24.11"),sQuery(id+"F0.wireOp",EDGE,"E13.25.0"),sQuery(id+"F0.wireOp",EDGE,"E13.25.1"),sQuery(id+"F0.wireOp",EDGE,"E13.25.2"),sQuery(id+"F0.wireOp",EDGE,"E13.25.3"),sQuery(id+"F0.wireOp",EDGE,"E13.25.4"),sQuery(id+"F0.wireOp",EDGE,"E13.25.5"),sQuery(id+"F0.wireOp",EDGE,"E13.25.6"),sQuery(id+"F0.wireOp",EDGE,"E13.25.7"),sQuery(id+"F0.wireOp",EDGE,"E13.25.8"),sQuery(id+"F0.wireOp",EDGE,"E13.25.9"),sQuery(id+"F0.wireOp",EDGE,"E13.25.10"),sQuery(id+"F0.wireOp",EDGE,"E13.25.11"),sQuery(id+"F0.wireOp",EDGE,"E13.26.0"),sQuery(id+"F0.wireOp",EDGE,"E13.26.1"),sQuery(id+"F0.wireOp",EDGE,"E13.26.2"),sQuery(id+"F0.wireOp",EDGE,"E13.26.3"),sQuery(id+"F0.wireOp",EDGE,"E13.26.4"),sQuery(id+"F0.wireOp",EDGE,"E13.26.5"),sQuery(id+"F0.wireOp",EDGE,"E13.26.6"),sQuery(id+"F0.wireOp",EDGE,"E13.26.7"),sQuery(id+"F0.wireOp",EDGE,"E13.26.8"),sQuery(id+"F0.wireOp",EDGE,"E13.26.9"),sQuery(id+"F0.wireOp",EDGE,"E13.26.10"),sQuery(id+"F0.wireOp",EDGE,"E13.26.11"),sQuery(id+"F0.wireOp",EDGE,"E13.27.0"),sQuery(id+"F0.wireOp",EDGE,"E13.27.1"),sQuery(id+"F0.wireOp",EDGE,"E13.27.2"),sQuery(id+"F0.wireOp",EDGE,"E13.27.3"),sQuery(id+"F0.wireOp",EDGE,"E13.27.4"),sQuery(id+"F0.wireOp",EDGE,"E13.27.5"),sQuery(id+"F0.wireOp",EDGE,"E13.27.6"),sQuery(id+"F0.wireOp",EDGE,"E13.27.7"),sQuery(id+"F0.wireOp",EDGE,"E13.27.8"),sQuery(id+"F0.wireOp",EDGE,"E13.27.9"),sQuery(id+"F0.wireOp",EDGE,"E13.27.10"),sQuery(id+"F0.wireOp",EDGE,"E13.27.11"),sQuery(id+"F0.wireOp",EDGE,"E13.28.0"),sQuery(id+"F0.wireOp",EDGE,"E13.28.1"),sQuery(id+"F0.wireOp",EDGE,"E13.28.2"),sQuery(id+"F0.wireOp",EDGE,"E13.28.3"),sQuery(id+"F0.wireOp",EDGE,"E13.28.4"),sQuery(id+"F0.wireOp",EDGE,"E13.28.5"),sQuery(id+"F0.wireOp",EDGE,"E13.28.6"),sQuery(id+"F0.wireOp",EDGE,"E13.28.7"),sQuery(id+"F0.wireOp",EDGE,"E13.28.8"),sQuery(id+"F0.wireOp",EDGE,"E13.28.9"),sQuery(id+"F0.wireOp",EDGE,"E13.28.10"),sQuery(id+"F0.wireOp",EDGE,"E13.28.11"),sQuery(id+"F0.wireOp",EDGE,"E13.29.0"),sQuery(id+"F0.wireOp",EDGE,"E13.29.1"),sQuery(id+"F0.wireOp",EDGE,"E13.29.2"),sQuery(id+"F0.wireOp",EDGE,"E13.29.3"),sQuery(id+"F0.wireOp",EDGE,"E13.29.4"),sQuery(id+"F0.wireOp",EDGE,"E13.29.5"),sQuery(id+"F0.wireOp",EDGE,"E13.29.6"),sQuery(id+"F0.wireOp",EDGE,"E13.29.7"),sQuery(id+"F0.wireOp",EDGE,"E13.29.8"),sQuery(id+"F0.wireOp",EDGE,"E13.29.9"),sQuery(id+"F0.wireOp",EDGE,"E13.29.10"),sQuery(id+"F0.wireOp",EDGE,"E13.29.11"),sQuery(id+"F0.wireOp",EDGE,"E13.30.0"),sQuery(id+"F0.wireOp",EDGE,"E13.30.1"),sQuery(id+"F0.wireOp",EDGE,"E13.30.2"),sQuery(id+"F0.wireOp",EDGE,"E13.30.3"),sQuery(id+"F0.wireOp",EDGE,"E13.30.4"),sQuery(id+"F0.wireOp",EDGE,"E13.30.5"),sQuery(id+"F0.wireOp",EDGE,"E13.30.6"),sQuery(id+"F0.wireOp",EDGE,"E13.30.7"),sQuery(id+"F0.wireOp",EDGE,"E13.30.8"),sQuery(id+"F0.wireOp",EDGE,"E13.30.9"),sQuery(id+"F0.wireOp",EDGE,"E13.30.10"),sQuery(id+"F0.wireOp",EDGE,"E13.30.11"),sQuery(id+"F0.wireOp",EDGE,"E13.31.0"),sQuery(id+"F0.wireOp",EDGE,"E13.31.1"),sQuery(id+"F0.wireOp",EDGE,"E13.31.2"),sQuery(id+"F0.wireOp",EDGE,"E13.31.3"),sQuery(id+"F0.wireOp",EDGE,"E13.31.4"),sQuery(id+"F0.wireOp",EDGE,"E13.31.5"),sQuery(id+"F0.wireOp",EDGE,"E13.31.6"),sQuery(id+"F0.wireOp",EDGE,"E13.31.7"),sQuery(id+"F0.wireOp",EDGE,"E13.31.8"),sQuery(id+"F0.wireOp",EDGE,"E13.31.9"),sQuery(id+"F0.wireOp",EDGE,"E13.31.10"),sQuery(id+"F0.wireOp",EDGE,"E13.31.11"),sQuery(id+"F0.wireOp",EDGE,"E13.32.0"),sQuery(id+"F0.wireOp",EDGE,"E13.32.1"),sQuery(id+"F0.wireOp",EDGE,"E13.32.2"),sQuery(id+"F0.wireOp",EDGE,"E13.32.3"),sQuery(id+"F0.wireOp",EDGE,"E13.32.4"),sQuery(id+"F0.wireOp",EDGE,"E13.32.5"),sQuery(id+"F0.wireOp",EDGE,"E13.32.6"),sQuery(id+"F0.wireOp",EDGE,"E13.32.7"),sQuery(id+"F0.wireOp",EDGE,"E13.32.8"),sQuery(id+"F0.wireOp",EDGE,"E13.32.9"),sQuery(id+"F0.wireOp",EDGE,"E13.32.10"),sQuery(id+"F0.wireOp",EDGE,"E13.32.11"),sQuery(id+"F0.wireOp",EDGE,"E13.33.0"),sQuery(id+"F0.wireOp",EDGE,"E13.33.1"),sQuery(id+"F0.wireOp",EDGE,"E13.33.2"),sQuery(id+"F0.wireOp",EDGE,"E13.33.3"),sQuery(id+"F0.wireOp",EDGE,"E13.33.4"),sQuery(id+"F0.wireOp",EDGE,"E13.33.5"),sQuery(id+"F0.wireOp",EDGE,"E13.33.6"),sQuery(id+"F0.wireOp",EDGE,"E13.33.7"),sQuery(id+"F0.wireOp",EDGE,"E13.33.8"),sQuery(id+"F0.wireOp",EDGE,"E13.33.9"),sQuery(id+"F0.wireOp",EDGE,"E13.33.10"),sQuery(id+"F0.wireOp",EDGE,"E13.33.11"),sQuery(id+"F0.wireOp",EDGE,"E13.34.0"),sQuery(id+"F0.wireOp",EDGE,"E13.34.1"),sQuery(id+"F0.wireOp",EDGE,"E13.34.2"),sQuery(id+"F0.wireOp",EDGE,"E13.34.3"),sQuery(id+"F0.wireOp",EDGE,"E13.34.4"),sQuery(id+"F0.wireOp",EDGE,"E13.34.5"),sQuery(id+"F0.wireOp",EDGE,"E13.34.6"),sQuery(id+"F0.wireOp",EDGE,"E13.34.7"),sQuery(id+"F0.wireOp",EDGE,"E13.34.8"),sQuery(id+"F0.wireOp",EDGE,"E13.34.9"),sQuery(id+"F0.wireOp",EDGE,"E13.34.10"),sQuery(id+"F0.wireOp",EDGE,"E13.34.11"),sQuery(id+"F0.wireOp",EDGE,"E13.35.0"),sQuery(id+"F0.wireOp",EDGE,"E13.35.1"),sQuery(id+"F0.wireOp",EDGE,"E13.35.2"),sQuery(id+"F0.wireOp",EDGE,"E13.35.3"),sQuery(id+"F0.wireOp",EDGE,"E13.35.4"),sQuery(id+"F0.wireOp",EDGE,"E13.35.5"),sQuery(id+"F0.wireOp",EDGE,"E13.35.6"),sQuery(id+"F0.wireOp",EDGE,"E13.35.7"),sQuery(id+"F0.wireOp",EDGE,"E13.35.8"),sQuery(id+"F0.wireOp",EDGE,"E13.35.9"),sQuery(id+"F0.wireOp",EDGE,"E13.35.10"),sQuery(id+"F0.wireOp",EDGE,"E13.35.11"),sQuery(id+"F0.wireOp",EDGE,"E14.trimOffspring"),sQuery(id+"F0.wireOp",EDGE,"E15.trimOffspring"),sQuery(id+"F0.wireOp",EDGE,"E16.trimOffspring"),sQuery(id+"F0.wireOp",EDGE,"E17.trimOffspring"),sQuery(id+"F0.wireOp",EDGE,"E18.trimOffspring"),sQuery(id+"F0.wireOp",EDGE,"E19.trimOffspring"),sQuery(id+"F0.wireOp",EDGE,"E20.trimOffspring"),sQuery(id+"F0.wireOp",EDGE,"E21.trimOffspring"),sQuery(id+"F0.wireOp",EDGE,"E22.trimOffspring"),sQuery(id+"F0.wireOp",EDGE,"E23.trimOffspring"),sQuery(id+"F0.wireOp",EDGE,"E24.trimOffspring"),sQuery(id+"F0.wireOp",EDGE,"E25.trimOffspring"),sQuery(id+"F0.wireOp",EDGE,"E26.trimOffspring"),sQuery(id+"F0.wireOp",EDGE,"E27.trimOffspring"),sQuery(id+"F0.wireOp",EDGE,"E28.trimOffspring"),sQuery(id+"F0.wireOp",EDGE,"E29.trimOffspring"),sQuery(id+"F0.wireOp",EDGE,"E30.trimOffspring"),sQuery(id+"F0.wireOp",EDGE,"E31.trimOffspring"),sQuery(id+"F0.wireOp",EDGE,"E32.trimOffspring"),sQuery(id+"F0.wireOp",EDGE,"E33.trimOffspring"),sQuery(id+"F0.wireOp",EDGE,"E34.trimOffspring"),sQuery(id+"F0.wireOp",EDGE,"E35.trimOffspring"),sQuery(id+"F0.wireOp",EDGE,"E36.trimOffspring"),sQuery(id+"F0.wireOp",EDGE,"E37.trimOffspring"),sQuery(id+"F0.wireOp",EDGE,"E38.trimOffspring"),sQuery(id+"F0.wireOp",EDGE,"E39.trimOffspring"),sQuery(id+"F0.wireOp",EDGE,"E40.trimOffspring"),sQuery(id+"F0.wireOp",EDGE,"E41.trimOffspring"),sQuery(id+"F0.wireOp",EDGE,"E42.trimOffspring"),sQuery(id+"F0.wireOp",EDGE,"E43.trimOffspring"),sQuery(id+"F0.wireOp",EDGE,"E44.trimOffspring"),sQuery(id+"F0.wireOp",EDGE,"E45.trimOffspring"),sQuery(id+"F0.wireOp",EDGE,"E46.trimOffspring"),sQuery(id+"F0.wireOp",EDGE,"E47.trimOffspring"),sQuery(id+"F0.wireOp",EDGE,"E48.trimOffspring")])],"isStart":false});
            shell(context, id + "F4", {"entities" : qUnion([Q0]), "thickness" : 6.35 * mm});
        }
        {
            var Q0;
            Q0=qCreatedBy(makeId("Right.planeOp"),FACE);
            cPlane(context, id + "F5", {"entities" : qUnion([Q0]), "cplaneType" : CPlaneType.OFFSET, "offset" : 9.52 * mm, "width" : 152.4 * mm, "height" : 152.4 * mm});
        }
        {
            var Q0;
            Q0=qCreatedBy(id+"F5.planeOp",FACE);
            var sketch = newSketch(context, id + "F6", { "sketchPlane" : qUnion([Q0])});
            skCircle(sketch, "E50", {"center": v(-9.53, 0) * mm, "radius": 1.13 * mm});
            skSolve(sketch);
        }
        {
            var Q0;
            Q0 = qSketchRegion(id + "F6", true);
            extrude(context, id + "F7", {"entities" : qUnion([Q0]), "operationType" : NewBodyOperationType.REMOVE, "oppositeDirection" : true, "depth" : 9.52 * mm});
        }
    });
